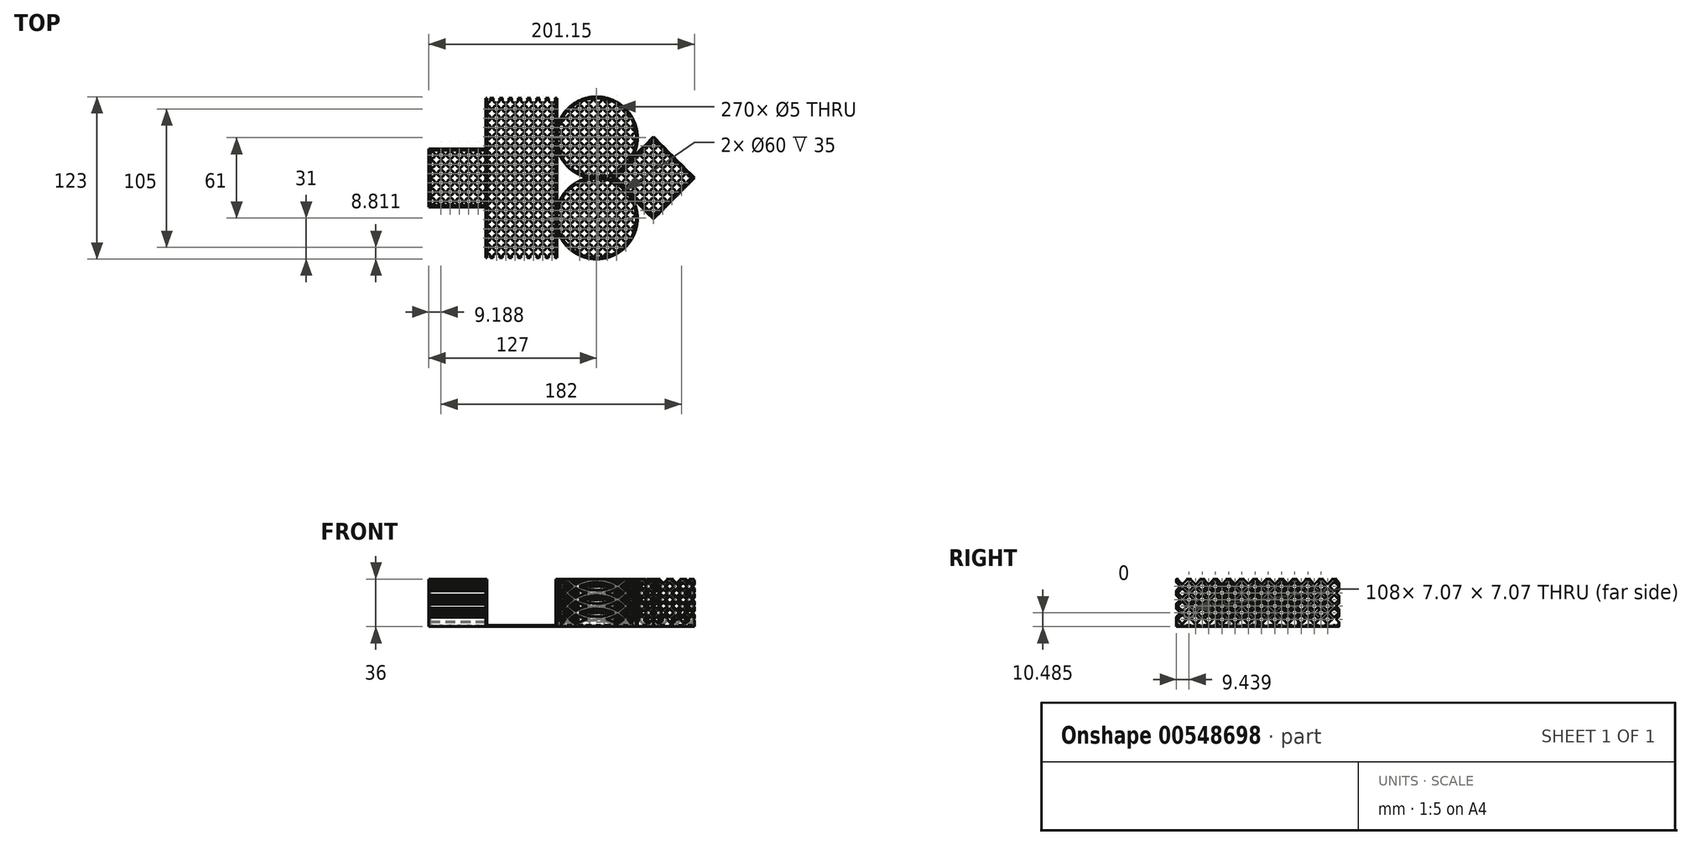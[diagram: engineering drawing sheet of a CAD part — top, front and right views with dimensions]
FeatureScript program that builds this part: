
annotation { "Feature Type Name" : "Feature", "Feature Type Description" : "" }
export const myFeature = defineFeature(function(context is Context, id is Id, definition is map)
    precondition{}
    {
        {
            assignVariable(context, id + "F0", {"name" : "thickness", "anyValue" : 1 * mm});
        }
        {
            var Q0;
            Q0=qCreatedBy(makeId("Top.planeOp"),FACE);
            var sketch = newSketch(context, id + "F1", { "sketchPlane" : qUnion([Q0])});
            skCircle(sketch, "E0", {"center": v(30, 30.5) * mm, "radius": 30 * mm});
            skCircle(sketch, "E1", {"center": v(30, -30.5) * mm, "radius": 30 * mm});
            skLineSegment(sketch, "E2.bottom", {"start": v(43.34, 0) * mm, "end": v(73.04, 29.7) * mm});
            skLineSegment(sketch, "E2.top", {"start": v(73.04, -29.7) * mm, "end": v(102.74, 0) * mm});
            skLineSegment(sketch, "E2.left", {"start": v(43.34, 0) * mm, "end": v(73.04, -29.7) * mm});
            skLineSegment(sketch, "E2.right", {"start": v(73.04, 29.7) * mm, "end": v(102.74, 0) * mm});
            skLineSegment(sketch, "E3.bottom", {"start": v(-53, 60.5) * mm, "end": v(-1, 60.5) * mm});
            skLineSegment(sketch, "E3.top", {"start": v(-53, -60.5) * mm, "end": v(-1, -60.5) * mm});
            skLineSegment(sketch, "E3.left", {"start": v(-53, 60.5) * mm, "end": v(-53, -60.5) * mm});
            skLineSegment(sketch, "E3.right", {"start": v(-1, 60.5) * mm, "end": v(-1, -60.5) * mm});
            skLineSegment(sketch, "E4.bottom", {"start": v(-96, 21) * mm, "end": v(-54, 21) * mm});
            skLineSegment(sketch, "E4.top", {"start": v(-96, -21) * mm, "end": v(-54, -21) * mm});
            skLineSegment(sketch, "E4.left", {"start": v(-96, 21) * mm, "end": v(-96, -21) * mm});
            skLineSegment(sketch, "E4.right", {"start": v(-54, 21) * mm, "end": v(-54, -21) * mm});
            skPoint(sketch, "E5", {"position": v(-96, 0) * mm});
            skSolve(sketch);
        }
        {
            var Q0;
            Q0 = qSketchRegion(id + "F1", true);
            extrude(context, id + "F2", {"entities" : qUnion([Q0]), "depth" : 35 * mm, "offsetDistance" : 25 * mm});
        }
        {
            var Q0;
            Q0=makeQuery(id+"F2.opExtrude","CAP_FACE",FACE,{"disambiguationData":[OSD([sQuery(id+"F1.wireOp",EDGE,"E1")])],"isStart":false});
            var Q1;
            Q1=makeQuery(id+"F2.opExtrude","CAP_FACE",FACE,{"disambiguationData":[OSD([sQuery(id+"F1.wireOp",EDGE,"E3.bottom"),sQuery(id+"F1.wireOp",EDGE,"E3.top"),sQuery(id+"F1.wireOp",EDGE,"E3.left"),sQuery(id+"F1.wireOp",EDGE,"E3.right")])],"isStart":false});
            var Q2;
            Q2=makeQuery(id+"F2.opExtrude","CAP_FACE",FACE,{"disambiguationData":[OSD([sQuery(id+"F1.wireOp",EDGE,"E0")])],"isStart":false});
            var Q3;
            Q3=makeQuery(id+"F2.opExtrude","CAP_FACE",FACE,{"disambiguationData":[OSD([sQuery(id+"F1.wireOp",EDGE,"E2.bottom"),sQuery(id+"F1.wireOp",EDGE,"E2.top"),sQuery(id+"F1.wireOp",EDGE,"E2.left"),sQuery(id+"F1.wireOp",EDGE,"E2.right")])],"isStart":false});
            var Q4;
            Q4=makeQuery(id+"F2.opExtrude","SWEPT_FACE",FACE,{"disambiguationData":[OSD([sQuery(id+"F1.wireOp",EDGE,"E3.bottom")])]});
            var Q5;
            Q5=makeQuery(id+"F2.opExtrude","SWEPT_FACE",FACE,{"disambiguationData":[OSD([sQuery(id+"F1.wireOp",EDGE,"E3.top")])]});
            var Q6;
            Q6=makeQuery(id+"F2.opExtrude","CAP_FACE",FACE,{"disambiguationData":[OSD([sQuery(id+"F1.wireOp",EDGE,"E4.bottom"),sQuery(id+"F1.wireOp",EDGE,"E4.top"),sQuery(id+"F1.wireOp",EDGE,"E4.left"),sQuery(id+"F1.wireOp",EDGE,"E4.right")])],"isStart":false});
            shell(context, id + "F3", {"entities" : qUnion([Q0, Q1, Q2, Q3, Q4, Q5, Q6]), "thickness" : (getVariable(context, 'thickness')), "oppositeDirection" : true});
        }
        {
            var Q0;
            Q0=makeQuery(id+"F2.opExtrude","SWEPT_FACE",FACE,{"disambiguationData":[OSD([sQuery(id+"F1.wireOp",EDGE,"E4.left")])]});
            var sketch = newSketch(context, id + "F4", { "sketchPlane" : qUnion([Q0])});
            skCircle(sketch, "E6", {"center": v(0, 21) * mm, "radius": 17 * mm});
            skLineSegment(sketch, "E7", {"start": v(-17, 21.3) * mm, "end": v(-16.76, 35) * mm});
            skLineSegment(sketch, "E8", {"start": v(17, 21) * mm, "end": v(17, 35) * mm});
            skLineSegment(sketch, "E9", {"start": v(-16.76, 35) * mm, "end": v(17, 35) * mm});
            skSolve(sketch);
        }
        {
            var Q0;
            Q0 = qSketchRegion(id + "F4", true);
            var Q1;
            Q1=makeQuery(id+"F3.opShell","OFFSET_FACE",FACE,{"disambiguationData":[OSD([sQuery(id+"F1.wireOp",EDGE,"E4.left")])]});
            extrude(context, id + "F5", {"entities" : qUnion([Q0]), "operationType" : NewBodyOperationType.REMOVE, "endBound" : BoundingType.UP_TO_SURFACE, "oppositeDirection" : true, "depth" : 25 * mm, "endBoundEntityFace" : qUnion([Q1]), "offsetDistance" : 25 * mm});
        }
        {
            var Q0;
            Q0=makeQuery(id+"F2.opExtrude","SWEPT_FACE",FACE,{"disambiguationData":[OSD([sQuery(id+"F1.wireOp",EDGE,"E2.top")])]});
            var sketch = newSketch(context, id + "F6", { "sketchPlane" : qUnion([Q0])});
            skCircle(sketch, "E10", {"center": v(51.65, 21) * mm, "radius": 17 * mm});
            skLineSegment(sketch, "E11", {"start": v(34.65, 21) * mm, "end": v(34.65, 35) * mm});
            skLineSegment(sketch, "E12", {"start": v(34.65, 35) * mm, "end": v(68.65, 35) * mm});
            skLineSegment(sketch, "E13", {"start": v(68.65, 35) * mm, "end": v(68.65, 21) * mm});
            skSolve(sketch);
        }
        {
            var Q0;
            Q0 = qSketchRegion(id + "F6", true);
            var Q1;
            Q1=makeQuery(id+"F3.opShell","OFFSET_FACE",FACE,{"disambiguationData":[OSD([sQuery(id+"F1.wireOp",EDGE,"E2.top")])]});
            extrude(context, id + "F7", {"entities" : qUnion([Q0]), "operationType" : NewBodyOperationType.REMOVE, "endBound" : BoundingType.UP_TO_SURFACE, "oppositeDirection" : true, "depth" : 25 * mm, "endBoundEntityFace" : qUnion([Q1]), "offsetDistance" : 25 * mm});
        }
        {
            var Q0;
            Q0=makeQuery(id+"F2.opExtrude","CAP_EDGE",EDGE,{"disambiguationData":[OSD([sQuery(id+"F1.wireOp",EDGE,"E3.top")])],"isStart":false});
            var Q1;
            {var subQ0=sQuery(id+"F1.wireOp",EDGE,"E3.top");Q1=makeQuery(id+"F3.opShell","OFFSET_EDGE",EDGE,{"disambiguationData":[OSD([subQ0]),TDD([makeQuery(id+"F2.opExtrude","CAP_EDGE",EDGE,{"disambiguationData":[OSD([subQ0])],"isStart":false})])]});}
            var Q2;
            Q2=makeQuery(id+"F5.boolean.opBoolean","COPY",EDGE,{"derivedFrom":makeQuery(id+"F5.opExtrude","SWEPT_EDGE",EDGE,{"disambiguationData":[OSD([sQuery(id+"F1.wireOp",EDGE,"E4.left"),sQuery(id+"F4.wireOp",EDGE,"E7"),sQuery(id+"F4.wireOp",EDGE,"E9")])]})});
            var Q3;
            Q3=makeQuery(id+"F5.boolean.opBoolean","COPY",EDGE,{"derivedFrom":makeQuery(id+"F5.opExtrude","SWEPT_EDGE",EDGE,{"disambiguationData":[OSD([sQuery(id+"F1.wireOp",EDGE,"E4.left"),sQuery(id+"F4.wireOp",EDGE,"E8"),sQuery(id+"F4.wireOp",EDGE,"E9")])]})});
            var Q4;
            Q4=makeQuery(id+"F2.opExtrude","CAP_EDGE",EDGE,{"disambiguationData":[OSD([sQuery(id+"F1.wireOp",EDGE,"E3.bottom")])],"isStart":false});
            var Q5;
            {var subQ0=sQuery(id+"F1.wireOp",EDGE,"E3.bottom");Q5=makeQuery(id+"F3.opShell","OFFSET_EDGE",EDGE,{"disambiguationData":[OSD([subQ0]),TDD([makeQuery(id+"F2.opExtrude","CAP_EDGE",EDGE,{"disambiguationData":[OSD([subQ0])],"isStart":false})])]});}
            var Q6;
            Q6=makeQuery(id+"F7.boolean.opBoolean","COPY",EDGE,{"derivedFrom":makeQuery(id+"F7.opExtrude","SWEPT_EDGE",EDGE,{"disambiguationData":[OSD([sQuery(id+"F1.wireOp",EDGE,"E2.top"),sQuery(id+"F6.wireOp",EDGE,"E11"),sQuery(id+"F6.wireOp",EDGE,"E12")])]})});
            var Q7;
            Q7=makeQuery(id+"F7.boolean.opBoolean","COPY",EDGE,{"derivedFrom":makeQuery(id+"F7.opExtrude","SWEPT_EDGE",EDGE,{"disambiguationData":[OSD([sQuery(id+"F1.wireOp",EDGE,"E2.top"),sQuery(id+"F6.wireOp",EDGE,"E12"),sQuery(id+"F6.wireOp",EDGE,"E13")])]})});
            fillet(context, id + "F8", {"entities" : qUnion([Q0, Q1, Q2, Q3, Q4, Q5, Q6, Q7]), "radius" : 5 * mm, "tangentPropagation" : true, "allowEdgeOverflow" : false});
        }
        {
            var Q0;
            Q0=makeQuery(id+"F2.opExtrude","SWEPT_BODY",BODY,{"disambiguationData":[OSD([sQuery(id+"F1.wireOp",EDGE,"E0")])]});
            var Q1;
            Q1=makeQuery(id+"F2.opExtrude","SWEPT_BODY",BODY,{"disambiguationData":[OSD([sQuery(id+"F1.wireOp",EDGE,"E1")])]});
            var Q2;
            Q2=makeQuery(id+"F2.opExtrude","SWEPT_BODY",BODY,{"disambiguationData":[OSD([sQuery(id+"F1.wireOp",EDGE,"E3.bottom"),sQuery(id+"F1.wireOp",EDGE,"E3.top"),sQuery(id+"F1.wireOp",EDGE,"E3.left"),sQuery(id+"F1.wireOp",EDGE,"E3.right")])]});
            var Q3;
            Q3=makeQuery(id+"F2.opExtrude","SWEPT_BODY",BODY,{"disambiguationData":[OSD([sQuery(id+"F1.wireOp",EDGE,"E2.bottom"),sQuery(id+"F1.wireOp",EDGE,"E2.top"),sQuery(id+"F1.wireOp",EDGE,"E2.left"),sQuery(id+"F1.wireOp",EDGE,"E2.right")])]});
            var Q4;
            Q4=makeQuery(id+"F2.opExtrude","SWEPT_BODY",BODY,{"disambiguationData":[OSD([sQuery(id+"F1.wireOp",EDGE,"E4.bottom"),sQuery(id+"F1.wireOp",EDGE,"E4.top"),sQuery(id+"F1.wireOp",EDGE,"E4.left"),sQuery(id+"F1.wireOp",EDGE,"E4.right")])]});
            booleanBodies(context, id + "F9", {"operationType" : BooleanOperationType.UNION, "tools" : qUnion([Q0, Q1, Q2, Q3, Q4])});
        }
        {
            var Q0;
            Q0=makeQuery(id+"F9.opBoolean","MERGE",FACE,{"derivedFrom":[makeQuery(id+"F2.opExtrude","CAP_FACE",FACE,{"disambiguationData":[OSD([sQuery(id+"F1.wireOp",EDGE,"E0")])],"isStart":true}),makeQuery(id+"F2.opExtrude","CAP_FACE",FACE,{"disambiguationData":[OSD([sQuery(id+"F1.wireOp",EDGE,"E1")])],"isStart":true}),makeQuery(id+"F2.opExtrude","CAP_FACE",FACE,{"disambiguationData":[OSD([sQuery(id+"F1.wireOp",EDGE,"E2.bottom"),sQuery(id+"F1.wireOp",EDGE,"E2.top"),sQuery(id+"F1.wireOp",EDGE,"E2.left"),sQuery(id+"F1.wireOp",EDGE,"E2.right")])],"isStart":true}),makeQuery(id+"F2.opExtrude","CAP_FACE",FACE,{"disambiguationData":[OSD([sQuery(id+"F1.wireOp",EDGE,"E3.bottom"),sQuery(id+"F1.wireOp",EDGE,"E3.top"),sQuery(id+"F1.wireOp",EDGE,"E3.left"),sQuery(id+"F1.wireOp",EDGE,"E3.right")])],"isStart":true}),makeQuery(id+"F2.opExtrude","CAP_FACE",FACE,{"disambiguationData":[OSD([sQuery(id+"F1.wireOp",EDGE,"E4.bottom"),sQuery(id+"F1.wireOp",EDGE,"E4.top"),sQuery(id+"F1.wireOp",EDGE,"E4.left"),sQuery(id+"F1.wireOp",EDGE,"E4.right")])],"isStart":true})]});
            var sketch = newSketch(context, id + "F10", { "sketchPlane" : qUnion([Q0])});
            skCircle(sketch, "E14", {"center": v(-101.81, -59.31) * mm, "radius": 2.5 * mm});
            skCircle(sketch, "E15.0.1.0", {"center": v(-101.81, -52.31) * mm, "radius": 2.5 * mm});
            skCircle(sketch, "E15.0.2.0", {"center": v(-101.81, -45.31) * mm, "radius": 2.5 * mm});
            skCircle(sketch, "E15.0.3.0", {"center": v(-101.81, -38.31) * mm, "radius": 2.5 * mm});
            skCircle(sketch, "E15.0.4.0", {"center": v(-101.81, -31.31) * mm, "radius": 2.5 * mm});
            skCircle(sketch, "E15.0.5.0", {"center": v(-101.81, -24.31) * mm, "radius": 2.5 * mm});
            skCircle(sketch, "E15.0.6.0", {"center": v(-101.81, -17.31) * mm, "radius": 2.5 * mm});
            skCircle(sketch, "E15.0.7.0", {"center": v(-101.81, -10.31) * mm, "radius": 2.5 * mm});
            skCircle(sketch, "E15.0.8.0", {"center": v(-101.81, -3.31) * mm, "radius": 2.5 * mm});
            skCircle(sketch, "E15.0.9.0", {"center": v(-101.81, 3.69) * mm, "radius": 2.5 * mm});
            skCircle(sketch, "E15.0.10.0", {"center": v(-101.81, 10.69) * mm, "radius": 2.5 * mm});
            skCircle(sketch, "E15.0.11.0", {"center": v(-101.81, 17.69) * mm, "radius": 2.5 * mm});
            skCircle(sketch, "E15.1.0.0", {"center": v(-94.81, -59.31) * mm, "radius": 2.5 * mm});
            skCircle(sketch, "E15.1.1.0", {"center": v(-94.81, -52.31) * mm, "radius": 2.5 * mm});
            skCircle(sketch, "E15.1.2.0", {"center": v(-94.81, -45.31) * mm, "radius": 2.5 * mm});
            skCircle(sketch, "E15.1.3.0", {"center": v(-94.81, -38.31) * mm, "radius": 2.5 * mm});
            skCircle(sketch, "E15.1.4.0", {"center": v(-94.81, -31.31) * mm, "radius": 2.5 * mm});
            skCircle(sketch, "E15.1.5.0", {"center": v(-94.81, -24.31) * mm, "radius": 2.5 * mm});
            skCircle(sketch, "E15.1.6.0", {"center": v(-94.81, -17.31) * mm, "radius": 2.5 * mm});
            skCircle(sketch, "E15.1.7.0", {"center": v(-94.81, -10.31) * mm, "radius": 2.5 * mm});
            skCircle(sketch, "E15.1.8.0", {"center": v(-94.81, -3.31) * mm, "radius": 2.5 * mm});
            skCircle(sketch, "E15.1.9.0", {"center": v(-94.81, 3.69) * mm, "radius": 2.5 * mm});
            skCircle(sketch, "E15.1.10.0", {"center": v(-94.81, 10.69) * mm, "radius": 2.5 * mm});
            skCircle(sketch, "E15.1.11.0", {"center": v(-94.81, 17.69) * mm, "radius": 2.5 * mm});
            skCircle(sketch, "E15.2.0.0", {"center": v(-87.81, -59.31) * mm, "radius": 2.5 * mm});
            skCircle(sketch, "E15.2.1.0", {"center": v(-87.81, -52.31) * mm, "radius": 2.5 * mm});
            skCircle(sketch, "E15.2.2.0", {"center": v(-87.81, -45.31) * mm, "radius": 2.5 * mm});
            skCircle(sketch, "E15.2.3.0", {"center": v(-87.81, -38.31) * mm, "radius": 2.5 * mm});
            skCircle(sketch, "E15.2.4.0", {"center": v(-87.81, -31.31) * mm, "radius": 2.5 * mm});
            skCircle(sketch, "E15.2.5.0", {"center": v(-87.81, -24.31) * mm, "radius": 2.5 * mm});
            skCircle(sketch, "E15.2.6.0", {"center": v(-87.81, -17.31) * mm, "radius": 2.5 * mm});
            skCircle(sketch, "E15.2.7.0", {"center": v(-87.81, -10.31) * mm, "radius": 2.5 * mm});
            skCircle(sketch, "E15.2.8.0", {"center": v(-87.81, -3.31) * mm, "radius": 2.5 * mm});
            skCircle(sketch, "E15.2.9.0", {"center": v(-87.81, 3.69) * mm, "radius": 2.5 * mm});
            skCircle(sketch, "E15.2.10.0", {"center": v(-87.81, 10.69) * mm, "radius": 2.5 * mm});
            skCircle(sketch, "E15.2.11.0", {"center": v(-87.81, 17.69) * mm, "radius": 2.5 * mm});
            skCircle(sketch, "E15.3.0.0", {"center": v(-80.81, -59.31) * mm, "radius": 2.5 * mm});
            skCircle(sketch, "E15.3.1.0", {"center": v(-80.81, -52.31) * mm, "radius": 2.5 * mm});
            skCircle(sketch, "E15.3.2.0", {"center": v(-80.81, -45.31) * mm, "radius": 2.5 * mm});
            skCircle(sketch, "E15.3.3.0", {"center": v(-80.81, -38.31) * mm, "radius": 2.5 * mm});
            skCircle(sketch, "E15.3.4.0", {"center": v(-80.81, -31.31) * mm, "radius": 2.5 * mm});
            skCircle(sketch, "E15.3.5.0", {"center": v(-80.81, -24.31) * mm, "radius": 2.5 * mm});
            skCircle(sketch, "E15.3.6.0", {"center": v(-80.81, -17.31) * mm, "radius": 2.5 * mm});
            skCircle(sketch, "E15.3.7.0", {"center": v(-80.81, -10.31) * mm, "radius": 2.5 * mm});
            skCircle(sketch, "E15.3.8.0", {"center": v(-80.81, -3.31) * mm, "radius": 2.5 * mm});
            skCircle(sketch, "E15.3.9.0", {"center": v(-80.81, 3.69) * mm, "radius": 2.5 * mm});
            skCircle(sketch, "E15.3.10.0", {"center": v(-80.81, 10.69) * mm, "radius": 2.5 * mm});
            skCircle(sketch, "E15.3.11.0", {"center": v(-80.81, 17.69) * mm, "radius": 2.5 * mm});
            skCircle(sketch, "E15.4.0.0", {"center": v(-73.81, -59.31) * mm, "radius": 2.5 * mm});
            skCircle(sketch, "E15.4.1.0", {"center": v(-73.81, -52.31) * mm, "radius": 2.5 * mm});
            skCircle(sketch, "E15.4.2.0", {"center": v(-73.81, -45.31) * mm, "radius": 2.5 * mm});
            skCircle(sketch, "E15.4.3.0", {"center": v(-73.81, -38.31) * mm, "radius": 2.5 * mm});
            skCircle(sketch, "E15.4.4.0", {"center": v(-73.81, -31.31) * mm, "radius": 2.5 * mm});
            skCircle(sketch, "E15.4.5.0", {"center": v(-73.81, -24.31) * mm, "radius": 2.5 * mm});
            skCircle(sketch, "E15.4.6.0", {"center": v(-73.81, -17.31) * mm, "radius": 2.5 * mm});
            skCircle(sketch, "E15.4.7.0", {"center": v(-73.81, -10.31) * mm, "radius": 2.5 * mm});
            skCircle(sketch, "E15.4.8.0", {"center": v(-73.81, -3.31) * mm, "radius": 2.5 * mm});
            skCircle(sketch, "E15.4.9.0", {"center": v(-73.81, 3.69) * mm, "radius": 2.5 * mm});
            skCircle(sketch, "E15.4.10.0", {"center": v(-73.81, 10.69) * mm, "radius": 2.5 * mm});
            skCircle(sketch, "E15.4.11.0", {"center": v(-73.81, 17.69) * mm, "radius": 2.5 * mm});
            skCircle(sketch, "E15.5.0.0", {"center": v(-66.81, -59.31) * mm, "radius": 2.5 * mm});
            skCircle(sketch, "E15.5.1.0", {"center": v(-66.81, -52.31) * mm, "radius": 2.5 * mm});
            skCircle(sketch, "E15.5.2.0", {"center": v(-66.81, -45.31) * mm, "radius": 2.5 * mm});
            skCircle(sketch, "E15.5.3.0", {"center": v(-66.81, -38.31) * mm, "radius": 2.5 * mm});
            skCircle(sketch, "E15.5.4.0", {"center": v(-66.81, -31.31) * mm, "radius": 2.5 * mm});
            skCircle(sketch, "E15.5.5.0", {"center": v(-66.81, -24.31) * mm, "radius": 2.5 * mm});
            skCircle(sketch, "E15.5.6.0", {"center": v(-66.81, -17.31) * mm, "radius": 2.5 * mm});
            skCircle(sketch, "E15.5.7.0", {"center": v(-66.81, -10.31) * mm, "radius": 2.5 * mm});
            skCircle(sketch, "E15.5.8.0", {"center": v(-66.81, -3.31) * mm, "radius": 2.5 * mm});
            skCircle(sketch, "E15.5.9.0", {"center": v(-66.81, 3.69) * mm, "radius": 2.5 * mm});
            skCircle(sketch, "E15.5.10.0", {"center": v(-66.81, 10.69) * mm, "radius": 2.5 * mm});
            skCircle(sketch, "E15.5.11.0", {"center": v(-66.81, 17.69) * mm, "radius": 2.5 * mm});
            skCircle(sketch, "E15.6.0.0", {"center": v(-59.81, -59.31) * mm, "radius": 2.5 * mm});
            skCircle(sketch, "E15.6.1.0", {"center": v(-59.81, -52.31) * mm, "radius": 2.5 * mm});
            skCircle(sketch, "E15.6.2.0", {"center": v(-59.81, -45.31) * mm, "radius": 2.5 * mm});
            skCircle(sketch, "E15.6.3.0", {"center": v(-59.81, -38.31) * mm, "radius": 2.5 * mm});
            skCircle(sketch, "E15.6.4.0", {"center": v(-59.81, -31.31) * mm, "radius": 2.5 * mm});
            skCircle(sketch, "E15.6.5.0", {"center": v(-59.81, -24.31) * mm, "radius": 2.5 * mm});
            skCircle(sketch, "E15.6.6.0", {"center": v(-59.81, -17.31) * mm, "radius": 2.5 * mm});
            skCircle(sketch, "E15.6.7.0", {"center": v(-59.81, -10.31) * mm, "radius": 2.5 * mm});
            skCircle(sketch, "E15.6.8.0", {"center": v(-59.81, -3.31) * mm, "radius": 2.5 * mm});
            skCircle(sketch, "E15.6.9.0", {"center": v(-59.81, 3.69) * mm, "radius": 2.5 * mm});
            skCircle(sketch, "E15.6.10.0", {"center": v(-59.81, 10.69) * mm, "radius": 2.5 * mm});
            skCircle(sketch, "E15.6.11.0", {"center": v(-59.81, 17.69) * mm, "radius": 2.5 * mm});
            skCircle(sketch, "E15.7.0.0", {"center": v(-52.81, -59.31) * mm, "radius": 2.5 * mm});
            skCircle(sketch, "E15.7.1.0", {"center": v(-52.81, -52.31) * mm, "radius": 2.5 * mm});
            skCircle(sketch, "E15.7.2.0", {"center": v(-52.81, -45.31) * mm, "radius": 2.5 * mm});
            skCircle(sketch, "E15.7.3.0", {"center": v(-52.81, -38.31) * mm, "radius": 2.5 * mm});
            skCircle(sketch, "E15.7.4.0", {"center": v(-52.81, -31.31) * mm, "radius": 2.5 * mm});
            skCircle(sketch, "E15.7.5.0", {"center": v(-52.81, -24.31) * mm, "radius": 2.5 * mm});
            skCircle(sketch, "E15.7.6.0", {"center": v(-52.81, -17.31) * mm, "radius": 2.5 * mm});
            skCircle(sketch, "E15.7.7.0", {"center": v(-52.81, -10.31) * mm, "radius": 2.5 * mm});
            skCircle(sketch, "E15.7.8.0", {"center": v(-52.81, -3.31) * mm, "radius": 2.5 * mm});
            skCircle(sketch, "E15.7.9.0", {"center": v(-52.81, 3.69) * mm, "radius": 2.5 * mm});
            skCircle(sketch, "E15.7.10.0", {"center": v(-52.81, 10.69) * mm, "radius": 2.5 * mm});
            skCircle(sketch, "E15.7.11.0", {"center": v(-52.81, 17.69) * mm, "radius": 2.5 * mm});
            skCircle(sketch, "E15.8.0.0", {"center": v(-45.81, -59.31) * mm, "radius": 2.5 * mm});
            skCircle(sketch, "E15.8.1.0", {"center": v(-45.81, -52.31) * mm, "radius": 2.5 * mm});
            skCircle(sketch, "E15.8.2.0", {"center": v(-45.81, -45.31) * mm, "radius": 2.5 * mm});
            skCircle(sketch, "E15.8.3.0", {"center": v(-45.81, -38.31) * mm, "radius": 2.5 * mm});
            skCircle(sketch, "E15.8.4.0", {"center": v(-45.81, -31.31) * mm, "radius": 2.5 * mm});
            skCircle(sketch, "E15.8.5.0", {"center": v(-45.81, -24.31) * mm, "radius": 2.5 * mm});
            skCircle(sketch, "E15.8.6.0", {"center": v(-45.81, -17.31) * mm, "radius": 2.5 * mm});
            skCircle(sketch, "E15.8.7.0", {"center": v(-45.81, -10.31) * mm, "radius": 2.5 * mm});
            skCircle(sketch, "E15.8.8.0", {"center": v(-45.81, -3.31) * mm, "radius": 2.5 * mm});
            skCircle(sketch, "E15.8.9.0", {"center": v(-45.81, 3.69) * mm, "radius": 2.5 * mm});
            skCircle(sketch, "E15.8.10.0", {"center": v(-45.81, 10.69) * mm, "radius": 2.5 * mm});
            skCircle(sketch, "E15.8.11.0", {"center": v(-45.81, 17.69) * mm, "radius": 2.5 * mm});
            skCircle(sketch, "E15.9.0.0", {"center": v(-38.81, -59.31) * mm, "radius": 2.5 * mm});
            skCircle(sketch, "E15.9.1.0", {"center": v(-38.81, -52.31) * mm, "radius": 2.5 * mm});
            skCircle(sketch, "E15.9.2.0", {"center": v(-38.81, -45.31) * mm, "radius": 2.5 * mm});
            skCircle(sketch, "E15.9.3.0", {"center": v(-38.81, -38.31) * mm, "radius": 2.5 * mm});
            skCircle(sketch, "E15.9.4.0", {"center": v(-38.81, -31.31) * mm, "radius": 2.5 * mm});
            skCircle(sketch, "E15.9.5.0", {"center": v(-38.81, -24.31) * mm, "radius": 2.5 * mm});
            skCircle(sketch, "E15.9.6.0", {"center": v(-38.81, -17.31) * mm, "radius": 2.5 * mm});
            skCircle(sketch, "E15.9.7.0", {"center": v(-38.81, -10.31) * mm, "radius": 2.5 * mm});
            skCircle(sketch, "E15.9.8.0", {"center": v(-38.81, -3.31) * mm, "radius": 2.5 * mm});
            skCircle(sketch, "E15.9.9.0", {"center": v(-38.81, 3.69) * mm, "radius": 2.5 * mm});
            skCircle(sketch, "E15.9.10.0", {"center": v(-38.81, 10.69) * mm, "radius": 2.5 * mm});
            skCircle(sketch, "E15.9.11.0", {"center": v(-38.81, 17.69) * mm, "radius": 2.5 * mm});
            skCircle(sketch, "E15.10.0.0", {"center": v(-31.81, -59.31) * mm, "radius": 2.5 * mm});
            skCircle(sketch, "E15.10.1.0", {"center": v(-31.81, -52.31) * mm, "radius": 2.5 * mm});
            skCircle(sketch, "E15.10.2.0", {"center": v(-31.81, -45.31) * mm, "radius": 2.5 * mm});
            skCircle(sketch, "E15.10.3.0", {"center": v(-31.81, -38.31) * mm, "radius": 2.5 * mm});
            skCircle(sketch, "E15.10.4.0", {"center": v(-31.81, -31.31) * mm, "radius": 2.5 * mm});
            skCircle(sketch, "E15.10.5.0", {"center": v(-31.81, -24.31) * mm, "radius": 2.5 * mm});
            skCircle(sketch, "E15.10.6.0", {"center": v(-31.81, -17.31) * mm, "radius": 2.5 * mm});
            skCircle(sketch, "E15.10.7.0", {"center": v(-31.81, -10.31) * mm, "radius": 2.5 * mm});
            skCircle(sketch, "E15.10.8.0", {"center": v(-31.81, -3.31) * mm, "radius": 2.5 * mm});
            skCircle(sketch, "E15.10.9.0", {"center": v(-31.81, 3.69) * mm, "radius": 2.5 * mm});
            skCircle(sketch, "E15.10.10.0", {"center": v(-31.81, 10.69) * mm, "radius": 2.5 * mm});
            skCircle(sketch, "E15.10.11.0", {"center": v(-31.81, 17.69) * mm, "radius": 2.5 * mm});
            skCircle(sketch, "E15.11.0.0", {"center": v(-24.81, -59.31) * mm, "radius": 2.5 * mm});
            skCircle(sketch, "E15.11.1.0", {"center": v(-24.81, -52.31) * mm, "radius": 2.5 * mm});
            skCircle(sketch, "E15.11.2.0", {"center": v(-24.81, -45.31) * mm, "radius": 2.5 * mm});
            skCircle(sketch, "E15.11.3.0", {"center": v(-24.81, -38.31) * mm, "radius": 2.5 * mm});
            skCircle(sketch, "E15.11.4.0", {"center": v(-24.81, -31.31) * mm, "radius": 2.5 * mm});
            skCircle(sketch, "E15.11.5.0", {"center": v(-24.81, -24.31) * mm, "radius": 2.5 * mm});
            skCircle(sketch, "E15.11.6.0", {"center": v(-24.81, -17.31) * mm, "radius": 2.5 * mm});
            skCircle(sketch, "E15.11.7.0", {"center": v(-24.81, -10.31) * mm, "radius": 2.5 * mm});
            skCircle(sketch, "E15.11.8.0", {"center": v(-24.81, -3.31) * mm, "radius": 2.5 * mm});
            skCircle(sketch, "E15.11.9.0", {"center": v(-24.81, 3.69) * mm, "radius": 2.5 * mm});
            skCircle(sketch, "E15.11.10.0", {"center": v(-24.81, 10.69) * mm, "radius": 2.5 * mm});
            skCircle(sketch, "E15.11.11.0", {"center": v(-24.81, 17.69) * mm, "radius": 2.5 * mm});
            skCircle(sketch, "E15.12.0.0", {"center": v(-17.81, -59.31) * mm, "radius": 2.5 * mm});
            skCircle(sketch, "E15.12.1.0", {"center": v(-17.81, -52.31) * mm, "radius": 2.5 * mm});
            skCircle(sketch, "E15.12.2.0", {"center": v(-17.81, -45.31) * mm, "radius": 2.5 * mm});
            skCircle(sketch, "E15.12.3.0", {"center": v(-17.81, -38.31) * mm, "radius": 2.5 * mm});
            skCircle(sketch, "E15.12.4.0", {"center": v(-17.81, -31.31) * mm, "radius": 2.5 * mm});
            skCircle(sketch, "E15.12.5.0", {"center": v(-17.81, -24.31) * mm, "radius": 2.5 * mm});
            skCircle(sketch, "E15.12.6.0", {"center": v(-17.81, -17.31) * mm, "radius": 2.5 * mm});
            skCircle(sketch, "E15.12.7.0", {"center": v(-17.81, -10.31) * mm, "radius": 2.5 * mm});
            skCircle(sketch, "E15.12.8.0", {"center": v(-17.81, -3.31) * mm, "radius": 2.5 * mm});
            skCircle(sketch, "E15.12.9.0", {"center": v(-17.81, 3.69) * mm, "radius": 2.5 * mm});
            skCircle(sketch, "E15.12.10.0", {"center": v(-17.81, 10.69) * mm, "radius": 2.5 * mm});
            skCircle(sketch, "E15.12.11.0", {"center": v(-17.81, 17.69) * mm, "radius": 2.5 * mm});
            skCircle(sketch, "E15.13.0.0", {"center": v(-10.81, -59.31) * mm, "radius": 2.5 * mm});
            skCircle(sketch, "E15.13.1.0", {"center": v(-10.81, -52.31) * mm, "radius": 2.5 * mm});
            skCircle(sketch, "E15.13.2.0", {"center": v(-10.81, -45.31) * mm, "radius": 2.5 * mm});
            skCircle(sketch, "E15.13.3.0", {"center": v(-10.81, -38.31) * mm, "radius": 2.5 * mm});
            skCircle(sketch, "E15.13.4.0", {"center": v(-10.81, -31.31) * mm, "radius": 2.5 * mm});
            skCircle(sketch, "E15.13.5.0", {"center": v(-10.81, -24.31) * mm, "radius": 2.5 * mm});
            skCircle(sketch, "E15.13.6.0", {"center": v(-10.81, -17.31) * mm, "radius": 2.5 * mm});
            skCircle(sketch, "E15.13.7.0", {"center": v(-10.81, -10.31) * mm, "radius": 2.5 * mm});
            skCircle(sketch, "E15.13.8.0", {"center": v(-10.81, -3.31) * mm, "radius": 2.5 * mm});
            skCircle(sketch, "E15.13.9.0", {"center": v(-10.81, 3.69) * mm, "radius": 2.5 * mm});
            skCircle(sketch, "E15.13.10.0", {"center": v(-10.81, 10.69) * mm, "radius": 2.5 * mm});
            skCircle(sketch, "E15.13.11.0", {"center": v(-10.81, 17.69) * mm, "radius": 2.5 * mm});
            skCircle(sketch, "E15.14.0.0", {"center": v(-3.81, -59.31) * mm, "radius": 2.5 * mm});
            skCircle(sketch, "E15.14.1.0", {"center": v(-3.81, -52.31) * mm, "radius": 2.5 * mm});
            skCircle(sketch, "E15.14.2.0", {"center": v(-3.81, -45.31) * mm, "radius": 2.5 * mm});
            skCircle(sketch, "E15.14.3.0", {"center": v(-3.81, -38.31) * mm, "radius": 2.5 * mm});
            skCircle(sketch, "E15.14.4.0", {"center": v(-3.81, -31.31) * mm, "radius": 2.5 * mm});
            skCircle(sketch, "E15.14.5.0", {"center": v(-3.81, -24.31) * mm, "radius": 2.5 * mm});
            skCircle(sketch, "E15.14.6.0", {"center": v(-3.81, -17.31) * mm, "radius": 2.5 * mm});
            skCircle(sketch, "E15.14.7.0", {"center": v(-3.81, -10.31) * mm, "radius": 2.5 * mm});
            skCircle(sketch, "E15.14.8.0", {"center": v(-3.81, -3.31) * mm, "radius": 2.5 * mm});
            skCircle(sketch, "E15.14.9.0", {"center": v(-3.81, 3.69) * mm, "radius": 2.5 * mm});
            skCircle(sketch, "E15.14.10.0", {"center": v(-3.81, 10.69) * mm, "radius": 2.5 * mm});
            skCircle(sketch, "E15.14.11.0", {"center": v(-3.81, 17.69) * mm, "radius": 2.5 * mm});
            skCircle(sketch, "E15.15.0.0", {"center": v(3.19, -59.31) * mm, "radius": 2.5 * mm});
            skCircle(sketch, "E15.15.1.0", {"center": v(3.19, -52.31) * mm, "radius": 2.5 * mm});
            skCircle(sketch, "E15.15.2.0", {"center": v(3.19, -45.31) * mm, "radius": 2.5 * mm});
            skCircle(sketch, "E15.15.3.0", {"center": v(3.19, -38.31) * mm, "radius": 2.5 * mm});
            skCircle(sketch, "E15.15.4.0", {"center": v(3.19, -31.31) * mm, "radius": 2.5 * mm});
            skCircle(sketch, "E15.15.5.0", {"center": v(3.19, -24.31) * mm, "radius": 2.5 * mm});
            skCircle(sketch, "E15.15.6.0", {"center": v(3.19, -17.31) * mm, "radius": 2.5 * mm});
            skCircle(sketch, "E15.15.7.0", {"center": v(3.19, -10.31) * mm, "radius": 2.5 * mm});
            skCircle(sketch, "E15.15.8.0", {"center": v(3.19, -3.31) * mm, "radius": 2.5 * mm});
            skCircle(sketch, "E15.15.9.0", {"center": v(3.19, 3.69) * mm, "radius": 2.5 * mm});
            skCircle(sketch, "E15.15.10.0", {"center": v(3.19, 10.69) * mm, "radius": 2.5 * mm});
            skCircle(sketch, "E15.15.11.0", {"center": v(3.19, 17.69) * mm, "radius": 2.5 * mm});
            skCircle(sketch, "E15.16.0.0", {"center": v(10.19, -59.31) * mm, "radius": 2.5 * mm});
            skCircle(sketch, "E15.16.1.0", {"center": v(10.19, -52.31) * mm, "radius": 2.5 * mm});
            skCircle(sketch, "E15.16.2.0", {"center": v(10.19, -45.31) * mm, "radius": 2.5 * mm});
            skCircle(sketch, "E15.16.3.0", {"center": v(10.19, -38.31) * mm, "radius": 2.5 * mm});
            skCircle(sketch, "E15.16.4.0", {"center": v(10.19, -31.31) * mm, "radius": 2.5 * mm});
            skCircle(sketch, "E15.16.5.0", {"center": v(10.19, -24.31) * mm, "radius": 2.5 * mm});
            skCircle(sketch, "E15.16.6.0", {"center": v(10.19, -17.31) * mm, "radius": 2.5 * mm});
            skCircle(sketch, "E15.16.7.0", {"center": v(10.19, -10.31) * mm, "radius": 2.5 * mm});
            skCircle(sketch, "E15.16.8.0", {"center": v(10.19, -3.31) * mm, "radius": 2.5 * mm});
            skCircle(sketch, "E15.16.9.0", {"center": v(10.19, 3.69) * mm, "radius": 2.5 * mm});
            skCircle(sketch, "E15.16.10.0", {"center": v(10.19, 10.69) * mm, "radius": 2.5 * mm});
            skCircle(sketch, "E15.16.11.0", {"center": v(10.19, 17.69) * mm, "radius": 2.5 * mm});
            skCircle(sketch, "E15.17.0.0", {"center": v(17.19, -59.31) * mm, "radius": 2.5 * mm});
            skCircle(sketch, "E15.17.1.0", {"center": v(17.19, -52.31) * mm, "radius": 2.5 * mm});
            skCircle(sketch, "E15.17.2.0", {"center": v(17.19, -45.31) * mm, "radius": 2.5 * mm});
            skCircle(sketch, "E15.17.3.0", {"center": v(17.19, -38.31) * mm, "radius": 2.5 * mm});
            skCircle(sketch, "E15.17.4.0", {"center": v(17.19, -31.31) * mm, "radius": 2.5 * mm});
            skCircle(sketch, "E15.17.5.0", {"center": v(17.19, -24.31) * mm, "radius": 2.5 * mm});
            skCircle(sketch, "E15.17.6.0", {"center": v(17.19, -17.31) * mm, "radius": 2.5 * mm});
            skCircle(sketch, "E15.17.7.0", {"center": v(17.19, -10.31) * mm, "radius": 2.5 * mm});
            skCircle(sketch, "E15.17.8.0", {"center": v(17.19, -3.31) * mm, "radius": 2.5 * mm});
            skCircle(sketch, "E15.17.9.0", {"center": v(17.19, 3.69) * mm, "radius": 2.5 * mm});
            skCircle(sketch, "E15.17.10.0", {"center": v(17.19, 10.69) * mm, "radius": 2.5 * mm});
            skCircle(sketch, "E15.17.11.0", {"center": v(17.19, 17.69) * mm, "radius": 2.5 * mm});
            skCircle(sketch, "E15.18.0.0", {"center": v(24.19, -59.31) * mm, "radius": 2.5 * mm});
            skCircle(sketch, "E15.18.1.0", {"center": v(24.19, -52.31) * mm, "radius": 2.5 * mm});
            skCircle(sketch, "E15.18.2.0", {"center": v(24.19, -45.31) * mm, "radius": 2.5 * mm});
            skCircle(sketch, "E15.18.3.0", {"center": v(24.19, -38.31) * mm, "radius": 2.5 * mm});
            skCircle(sketch, "E15.18.4.0", {"center": v(24.19, -31.31) * mm, "radius": 2.5 * mm});
            skCircle(sketch, "E15.18.5.0", {"center": v(24.19, -24.31) * mm, "radius": 2.5 * mm});
            skCircle(sketch, "E15.18.6.0", {"center": v(24.19, -17.31) * mm, "radius": 2.5 * mm});
            skCircle(sketch, "E15.18.7.0", {"center": v(24.19, -10.31) * mm, "radius": 2.5 * mm});
            skCircle(sketch, "E15.18.8.0", {"center": v(24.19, -3.31) * mm, "radius": 2.5 * mm});
            skCircle(sketch, "E15.18.9.0", {"center": v(24.19, 3.69) * mm, "radius": 2.5 * mm});
            skCircle(sketch, "E15.18.10.0", {"center": v(24.19, 10.69) * mm, "radius": 2.5 * mm});
            skCircle(sketch, "E15.18.11.0", {"center": v(24.19, 17.69) * mm, "radius": 2.5 * mm});
            skCircle(sketch, "E15.19.0.0", {"center": v(31.19, -59.31) * mm, "radius": 2.5 * mm});
            skCircle(sketch, "E15.19.1.0", {"center": v(31.19, -52.31) * mm, "radius": 2.5 * mm});
            skCircle(sketch, "E15.19.2.0", {"center": v(31.19, -45.31) * mm, "radius": 2.5 * mm});
            skCircle(sketch, "E15.19.3.0", {"center": v(31.19, -38.31) * mm, "radius": 2.5 * mm});
            skCircle(sketch, "E15.19.4.0", {"center": v(31.19, -31.31) * mm, "radius": 2.5 * mm});
            skCircle(sketch, "E15.19.5.0", {"center": v(31.19, -24.31) * mm, "radius": 2.5 * mm});
            skCircle(sketch, "E15.19.6.0", {"center": v(31.19, -17.31) * mm, "radius": 2.5 * mm});
            skCircle(sketch, "E15.19.7.0", {"center": v(31.19, -10.31) * mm, "radius": 2.5 * mm});
            skCircle(sketch, "E15.19.8.0", {"center": v(31.19, -3.31) * mm, "radius": 2.5 * mm});
            skCircle(sketch, "E15.19.9.0", {"center": v(31.19, 3.69) * mm, "radius": 2.5 * mm});
            skCircle(sketch, "E15.19.10.0", {"center": v(31.19, 10.69) * mm, "radius": 2.5 * mm});
            skCircle(sketch, "E15.19.11.0", {"center": v(31.19, 17.69) * mm, "radius": 2.5 * mm});
            skLineSegment(sketch, "E15.direction1", {"start": v(-101.81, -59.31) * mm, "end": v(-94.81, -59.31) * mm, "construction": true});
            skLineSegment(sketch, "E15.direction2", {"start": v(-101.81, -59.31) * mm, "end": v(-101.81, -52.31) * mm, "construction": true});
            skCircle(sketch, "E16.0.20.0", {"center": v(38.19, -59.31) * mm, "radius": 2.5 * mm});
            skCircle(sketch, "E16.0.20.1", {"center": v(38.19, -52.31) * mm, "radius": 2.5 * mm});
            skCircle(sketch, "E16.0.20.2", {"center": v(38.19, -45.31) * mm, "radius": 2.5 * mm});
            skCircle(sketch, "E16.0.20.3", {"center": v(38.19, -38.31) * mm, "radius": 2.5 * mm});
            skCircle(sketch, "E16.0.20.4", {"center": v(38.19, -31.31) * mm, "radius": 2.5 * mm});
            skCircle(sketch, "E16.0.20.5", {"center": v(38.19, -24.31) * mm, "radius": 2.5 * mm});
            skCircle(sketch, "E16.0.20.6", {"center": v(38.19, -17.31) * mm, "radius": 2.5 * mm});
            skCircle(sketch, "E16.0.20.7", {"center": v(38.19, -10.31) * mm, "radius": 2.5 * mm});
            skCircle(sketch, "E16.0.20.8", {"center": v(38.19, -3.31) * mm, "radius": 2.5 * mm});
            skCircle(sketch, "E16.0.20.9", {"center": v(38.19, 3.69) * mm, "radius": 2.5 * mm});
            skCircle(sketch, "E16.0.20.10", {"center": v(38.19, 10.69) * mm, "radius": 2.5 * mm});
            skCircle(sketch, "E16.0.20.11", {"center": v(38.19, 17.69) * mm, "radius": 2.5 * mm});
            skCircle(sketch, "E16.0.21.0", {"center": v(45.19, -59.31) * mm, "radius": 2.5 * mm});
            skCircle(sketch, "E16.0.21.1", {"center": v(45.19, -52.31) * mm, "radius": 2.5 * mm});
            skCircle(sketch, "E16.0.21.2", {"center": v(45.19, -45.31) * mm, "radius": 2.5 * mm});
            skCircle(sketch, "E16.0.21.3", {"center": v(45.19, -38.31) * mm, "radius": 2.5 * mm});
            skCircle(sketch, "E16.0.21.4", {"center": v(45.19, -31.31) * mm, "radius": 2.5 * mm});
            skCircle(sketch, "E16.0.21.5", {"center": v(45.19, -24.31) * mm, "radius": 2.5 * mm});
            skCircle(sketch, "E16.0.21.6", {"center": v(45.19, -17.31) * mm, "radius": 2.5 * mm});
            skCircle(sketch, "E16.0.21.7", {"center": v(45.19, -10.31) * mm, "radius": 2.5 * mm});
            skCircle(sketch, "E16.0.21.8", {"center": v(45.19, -3.31) * mm, "radius": 2.5 * mm});
            skCircle(sketch, "E16.0.21.9", {"center": v(45.19, 3.69) * mm, "radius": 2.5 * mm});
            skCircle(sketch, "E16.0.21.10", {"center": v(45.19, 10.69) * mm, "radius": 2.5 * mm});
            skCircle(sketch, "E16.0.21.11", {"center": v(45.19, 17.69) * mm, "radius": 2.5 * mm});
            skCircle(sketch, "E17.0.22.0", {"center": v(52.19, -59.31) * mm, "radius": 2.5 * mm});
            skCircle(sketch, "E17.0.22.1", {"center": v(52.19, -52.31) * mm, "radius": 2.5 * mm});
            skCircle(sketch, "E17.0.22.2", {"center": v(52.19, -45.31) * mm, "radius": 2.5 * mm});
            skCircle(sketch, "E17.0.22.3", {"center": v(52.19, -38.31) * mm, "radius": 2.5 * mm});
            skCircle(sketch, "E17.0.22.4", {"center": v(52.19, -31.31) * mm, "radius": 2.5 * mm});
            skCircle(sketch, "E17.0.22.5", {"center": v(52.19, -24.31) * mm, "radius": 2.5 * mm});
            skCircle(sketch, "E17.0.22.6", {"center": v(52.19, -17.31) * mm, "radius": 2.5 * mm});
            skCircle(sketch, "E17.0.22.7", {"center": v(52.19, -10.31) * mm, "radius": 2.5 * mm});
            skCircle(sketch, "E17.0.22.8", {"center": v(52.19, -3.31) * mm, "radius": 2.5 * mm});
            skCircle(sketch, "E17.0.22.9", {"center": v(52.19, 3.69) * mm, "radius": 2.5 * mm});
            skCircle(sketch, "E17.0.22.10", {"center": v(52.19, 10.69) * mm, "radius": 2.5 * mm});
            skCircle(sketch, "E17.0.22.11", {"center": v(52.19, 17.69) * mm, "radius": 2.5 * mm});
            skCircle(sketch, "E17.0.23.0", {"center": v(59.19, -59.31) * mm, "radius": 2.5 * mm});
            skCircle(sketch, "E17.0.23.1", {"center": v(59.19, -52.31) * mm, "radius": 2.5 * mm});
            skCircle(sketch, "E17.0.23.2", {"center": v(59.19, -45.31) * mm, "radius": 2.5 * mm});
            skCircle(sketch, "E17.0.23.3", {"center": v(59.19, -38.31) * mm, "radius": 2.5 * mm});
            skCircle(sketch, "E17.0.23.4", {"center": v(59.19, -31.31) * mm, "radius": 2.5 * mm});
            skCircle(sketch, "E17.0.23.5", {"center": v(59.19, -24.31) * mm, "radius": 2.5 * mm});
            skCircle(sketch, "E17.0.23.6", {"center": v(59.19, -17.31) * mm, "radius": 2.5 * mm});
            skCircle(sketch, "E17.0.23.7", {"center": v(59.19, -10.31) * mm, "radius": 2.5 * mm});
            skCircle(sketch, "E17.0.23.8", {"center": v(59.19, -3.31) * mm, "radius": 2.5 * mm});
            skCircle(sketch, "E17.0.23.9", {"center": v(59.19, 3.69) * mm, "radius": 2.5 * mm});
            skCircle(sketch, "E17.0.23.10", {"center": v(59.19, 10.69) * mm, "radius": 2.5 * mm});
            skCircle(sketch, "E17.0.23.11", {"center": v(59.19, 17.69) * mm, "radius": 2.5 * mm});
            skCircle(sketch, "E17.0.24.0", {"center": v(66.19, -59.31) * mm, "radius": 2.5 * mm});
            skCircle(sketch, "E17.0.24.1", {"center": v(66.19, -52.31) * mm, "radius": 2.5 * mm});
            skCircle(sketch, "E17.0.24.2", {"center": v(66.19, -45.31) * mm, "radius": 2.5 * mm});
            skCircle(sketch, "E17.0.24.3", {"center": v(66.19, -38.31) * mm, "radius": 2.5 * mm});
            skCircle(sketch, "E17.0.24.4", {"center": v(66.19, -31.31) * mm, "radius": 2.5 * mm});
            skCircle(sketch, "E17.0.24.5", {"center": v(66.19, -24.31) * mm, "radius": 2.5 * mm});
            skCircle(sketch, "E17.0.24.6", {"center": v(66.19, -17.31) * mm, "radius": 2.5 * mm});
            skCircle(sketch, "E17.0.24.7", {"center": v(66.19, -10.31) * mm, "radius": 2.5 * mm});
            skCircle(sketch, "E17.0.24.8", {"center": v(66.19, -3.31) * mm, "radius": 2.5 * mm});
            skCircle(sketch, "E17.0.24.9", {"center": v(66.19, 3.69) * mm, "radius": 2.5 * mm});
            skCircle(sketch, "E17.0.24.10", {"center": v(66.19, 10.69) * mm, "radius": 2.5 * mm});
            skCircle(sketch, "E17.0.24.11", {"center": v(66.19, 17.69) * mm, "radius": 2.5 * mm});
            skCircle(sketch, "E17.0.25.0", {"center": v(73.19, -59.31) * mm, "radius": 2.5 * mm});
            skCircle(sketch, "E17.0.25.1", {"center": v(73.19, -52.31) * mm, "radius": 2.5 * mm});
            skCircle(sketch, "E17.0.25.2", {"center": v(73.19, -45.31) * mm, "radius": 2.5 * mm});
            skCircle(sketch, "E17.0.25.3", {"center": v(73.19, -38.31) * mm, "radius": 2.5 * mm});
            skCircle(sketch, "E17.0.25.4", {"center": v(73.19, -31.31) * mm, "radius": 2.5 * mm});
            skCircle(sketch, "E17.0.25.5", {"center": v(73.19, -24.31) * mm, "radius": 2.5 * mm});
            skCircle(sketch, "E17.0.25.6", {"center": v(73.19, -17.31) * mm, "radius": 2.5 * mm});
            skCircle(sketch, "E17.0.25.7", {"center": v(73.19, -10.31) * mm, "radius": 2.5 * mm});
            skCircle(sketch, "E17.0.25.8", {"center": v(73.19, -3.31) * mm, "radius": 2.5 * mm});
            skCircle(sketch, "E17.0.25.9", {"center": v(73.19, 3.69) * mm, "radius": 2.5 * mm});
            skCircle(sketch, "E17.0.25.10", {"center": v(73.19, 10.69) * mm, "radius": 2.5 * mm});
            skCircle(sketch, "E17.0.25.11", {"center": v(73.19, 17.69) * mm, "radius": 2.5 * mm});
            skCircle(sketch, "E17.0.26.0", {"center": v(80.19, -59.31) * mm, "radius": 2.5 * mm});
            skCircle(sketch, "E17.0.26.1", {"center": v(80.19, -52.31) * mm, "radius": 2.5 * mm});
            skCircle(sketch, "E17.0.26.2", {"center": v(80.19, -45.31) * mm, "radius": 2.5 * mm});
            skCircle(sketch, "E17.0.26.3", {"center": v(80.19, -38.31) * mm, "radius": 2.5 * mm});
            skCircle(sketch, "E17.0.26.4", {"center": v(80.19, -31.31) * mm, "radius": 2.5 * mm});
            skCircle(sketch, "E17.0.26.5", {"center": v(80.19, -24.31) * mm, "radius": 2.5 * mm});
            skCircle(sketch, "E17.0.26.6", {"center": v(80.19, -17.31) * mm, "radius": 2.5 * mm});
            skCircle(sketch, "E17.0.26.7", {"center": v(80.19, -10.31) * mm, "radius": 2.5 * mm});
            skCircle(sketch, "E17.0.26.8", {"center": v(80.19, -3.31) * mm, "radius": 2.5 * mm});
            skCircle(sketch, "E17.0.26.9", {"center": v(80.19, 3.69) * mm, "radius": 2.5 * mm});
            skCircle(sketch, "E17.0.26.10", {"center": v(80.19, 10.69) * mm, "radius": 2.5 * mm});
            skCircle(sketch, "E17.0.26.11", {"center": v(80.19, 17.69) * mm, "radius": 2.5 * mm});
            skCircle(sketch, "E17.0.27.0", {"center": v(87.19, -59.31) * mm, "radius": 2.5 * mm});
            skCircle(sketch, "E17.0.27.1", {"center": v(87.19, -52.31) * mm, "radius": 2.5 * mm});
            skCircle(sketch, "E17.0.27.2", {"center": v(87.19, -45.31) * mm, "radius": 2.5 * mm});
            skCircle(sketch, "E17.0.27.3", {"center": v(87.19, -38.31) * mm, "radius": 2.5 * mm});
            skCircle(sketch, "E17.0.27.4", {"center": v(87.19, -31.31) * mm, "radius": 2.5 * mm});
            skCircle(sketch, "E17.0.27.5", {"center": v(87.19, -24.31) * mm, "radius": 2.5 * mm});
            skCircle(sketch, "E17.0.27.6", {"center": v(87.19, -17.31) * mm, "radius": 2.5 * mm});
            skCircle(sketch, "E17.0.27.7", {"center": v(87.19, -10.31) * mm, "radius": 2.5 * mm});
            skCircle(sketch, "E17.0.27.8", {"center": v(87.19, -3.31) * mm, "radius": 2.5 * mm});
            skCircle(sketch, "E17.0.27.9", {"center": v(87.19, 3.69) * mm, "radius": 2.5 * mm});
            skCircle(sketch, "E17.0.27.10", {"center": v(87.19, 10.69) * mm, "radius": 2.5 * mm});
            skCircle(sketch, "E17.0.27.11", {"center": v(87.19, 17.69) * mm, "radius": 2.5 * mm});
            skCircle(sketch, "E17.0.28.0", {"center": v(94.19, -59.31) * mm, "radius": 2.5 * mm});
            skCircle(sketch, "E17.0.28.1", {"center": v(94.19, -52.31) * mm, "radius": 2.5 * mm});
            skCircle(sketch, "E17.0.28.2", {"center": v(94.19, -45.31) * mm, "radius": 2.5 * mm});
            skCircle(sketch, "E17.0.28.3", {"center": v(94.19, -38.31) * mm, "radius": 2.5 * mm});
            skCircle(sketch, "E17.0.28.4", {"center": v(94.19, -31.31) * mm, "radius": 2.5 * mm});
            skCircle(sketch, "E17.0.28.5", {"center": v(94.19, -24.31) * mm, "radius": 2.5 * mm});
            skCircle(sketch, "E17.0.28.6", {"center": v(94.19, -17.31) * mm, "radius": 2.5 * mm});
            skCircle(sketch, "E17.0.28.7", {"center": v(94.19, -10.31) * mm, "radius": 2.5 * mm});
            skCircle(sketch, "E17.0.28.8", {"center": v(94.19, -3.31) * mm, "radius": 2.5 * mm});
            skCircle(sketch, "E17.0.28.9", {"center": v(94.19, 3.69) * mm, "radius": 2.5 * mm});
            skCircle(sketch, "E17.0.28.10", {"center": v(94.19, 10.69) * mm, "radius": 2.5 * mm});
            skCircle(sketch, "E17.0.28.11", {"center": v(94.19, 17.69) * mm, "radius": 2.5 * mm});
            skCircle(sketch, "E17.0.29.0", {"center": v(101.19, -59.31) * mm, "radius": 2.5 * mm});
            skCircle(sketch, "E17.0.29.1", {"center": v(101.19, -52.31) * mm, "radius": 2.5 * mm});
            skCircle(sketch, "E17.0.29.2", {"center": v(101.19, -45.31) * mm, "radius": 2.5 * mm});
            skCircle(sketch, "E17.0.29.3", {"center": v(101.19, -38.31) * mm, "radius": 2.5 * mm});
            skCircle(sketch, "E17.0.29.4", {"center": v(101.19, -31.31) * mm, "radius": 2.5 * mm});
            skCircle(sketch, "E17.0.29.5", {"center": v(101.19, -24.31) * mm, "radius": 2.5 * mm});
            skCircle(sketch, "E17.0.29.6", {"center": v(101.19, -17.31) * mm, "radius": 2.5 * mm});
            skCircle(sketch, "E17.0.29.7", {"center": v(101.19, -10.31) * mm, "radius": 2.5 * mm});
            skCircle(sketch, "E17.0.29.8", {"center": v(101.19, -3.31) * mm, "radius": 2.5 * mm});
            skCircle(sketch, "E17.0.29.9", {"center": v(101.19, 3.69) * mm, "radius": 2.5 * mm});
            skCircle(sketch, "E17.0.29.10", {"center": v(101.19, 10.69) * mm, "radius": 2.5 * mm});
            skCircle(sketch, "E17.0.29.11", {"center": v(101.19, 17.69) * mm, "radius": 2.5 * mm});
            skCircle(sketch, "E18.0.0.12", {"center": v(-101.81, 24.69) * mm, "radius": 2.5 * mm});
            skCircle(sketch, "E18.0.0.13", {"center": v(-101.81, 31.69) * mm, "radius": 2.5 * mm});
            skCircle(sketch, "E18.0.0.14", {"center": v(-101.81, 38.69) * mm, "radius": 2.5 * mm});
            skCircle(sketch, "E18.0.0.15", {"center": v(-101.81, 45.69) * mm, "radius": 2.5 * mm});
            skCircle(sketch, "E18.0.0.16", {"center": v(-101.81, 52.69) * mm, "radius": 2.5 * mm});
            skCircle(sketch, "E18.0.0.17", {"center": v(-101.81, 59.69) * mm, "radius": 2.5 * mm});
            skCircle(sketch, "E18.0.1.12", {"center": v(-94.81, 24.69) * mm, "radius": 2.5 * mm});
            skCircle(sketch, "E18.0.1.13", {"center": v(-94.81, 31.69) * mm, "radius": 2.5 * mm});
            skCircle(sketch, "E18.0.1.14", {"center": v(-94.81, 38.69) * mm, "radius": 2.5 * mm});
            skCircle(sketch, "E18.0.1.15", {"center": v(-94.81, 45.69) * mm, "radius": 2.5 * mm});
            skCircle(sketch, "E18.0.1.16", {"center": v(-94.81, 52.69) * mm, "radius": 2.5 * mm});
            skCircle(sketch, "E18.0.1.17", {"center": v(-94.81, 59.69) * mm, "radius": 2.5 * mm});
            skCircle(sketch, "E18.0.2.12", {"center": v(-87.81, 24.69) * mm, "radius": 2.5 * mm});
            skCircle(sketch, "E18.0.2.13", {"center": v(-87.81, 31.69) * mm, "radius": 2.5 * mm});
            skCircle(sketch, "E18.0.2.14", {"center": v(-87.81, 38.69) * mm, "radius": 2.5 * mm});
            skCircle(sketch, "E18.0.2.15", {"center": v(-87.81, 45.69) * mm, "radius": 2.5 * mm});
            skCircle(sketch, "E18.0.2.16", {"center": v(-87.81, 52.69) * mm, "radius": 2.5 * mm});
            skCircle(sketch, "E18.0.2.17", {"center": v(-87.81, 59.69) * mm, "radius": 2.5 * mm});
            skCircle(sketch, "E18.0.3.12", {"center": v(-80.81, 24.69) * mm, "radius": 2.5 * mm});
            skCircle(sketch, "E18.0.3.13", {"center": v(-80.81, 31.69) * mm, "radius": 2.5 * mm});
            skCircle(sketch, "E18.0.3.14", {"center": v(-80.81, 38.69) * mm, "radius": 2.5 * mm});
            skCircle(sketch, "E18.0.3.15", {"center": v(-80.81, 45.69) * mm, "radius": 2.5 * mm});
            skCircle(sketch, "E18.0.3.16", {"center": v(-80.81, 52.69) * mm, "radius": 2.5 * mm});
            skCircle(sketch, "E18.0.3.17", {"center": v(-80.81, 59.69) * mm, "radius": 2.5 * mm});
            skCircle(sketch, "E18.0.4.12", {"center": v(-73.81, 24.69) * mm, "radius": 2.5 * mm});
            skCircle(sketch, "E18.0.4.13", {"center": v(-73.81, 31.69) * mm, "radius": 2.5 * mm});
            skCircle(sketch, "E18.0.4.14", {"center": v(-73.81, 38.69) * mm, "radius": 2.5 * mm});
            skCircle(sketch, "E18.0.4.15", {"center": v(-73.81, 45.69) * mm, "radius": 2.5 * mm});
            skCircle(sketch, "E18.0.4.16", {"center": v(-73.81, 52.69) * mm, "radius": 2.5 * mm});
            skCircle(sketch, "E18.0.4.17", {"center": v(-73.81, 59.69) * mm, "radius": 2.5 * mm});
            skCircle(sketch, "E18.0.5.12", {"center": v(-66.81, 24.69) * mm, "radius": 2.5 * mm});
            skCircle(sketch, "E18.0.5.13", {"center": v(-66.81, 31.69) * mm, "radius": 2.5 * mm});
            skCircle(sketch, "E18.0.5.14", {"center": v(-66.81, 38.69) * mm, "radius": 2.5 * mm});
            skCircle(sketch, "E18.0.5.15", {"center": v(-66.81, 45.69) * mm, "radius": 2.5 * mm});
            skCircle(sketch, "E18.0.5.16", {"center": v(-66.81, 52.69) * mm, "radius": 2.5 * mm});
            skCircle(sketch, "E18.0.5.17", {"center": v(-66.81, 59.69) * mm, "radius": 2.5 * mm});
            skCircle(sketch, "E18.0.6.12", {"center": v(-59.81, 24.69) * mm, "radius": 2.5 * mm});
            skCircle(sketch, "E18.0.6.13", {"center": v(-59.81, 31.69) * mm, "radius": 2.5 * mm});
            skCircle(sketch, "E18.0.6.14", {"center": v(-59.81, 38.69) * mm, "radius": 2.5 * mm});
            skCircle(sketch, "E18.0.6.15", {"center": v(-59.81, 45.69) * mm, "radius": 2.5 * mm});
            skCircle(sketch, "E18.0.6.16", {"center": v(-59.81, 52.69) * mm, "radius": 2.5 * mm});
            skCircle(sketch, "E18.0.6.17", {"center": v(-59.81, 59.69) * mm, "radius": 2.5 * mm});
            skCircle(sketch, "E18.0.7.12", {"center": v(-52.81, 24.69) * mm, "radius": 2.5 * mm});
            skCircle(sketch, "E18.0.7.13", {"center": v(-52.81, 31.69) * mm, "radius": 2.5 * mm});
            skCircle(sketch, "E18.0.7.14", {"center": v(-52.81, 38.69) * mm, "radius": 2.5 * mm});
            skCircle(sketch, "E18.0.7.15", {"center": v(-52.81, 45.69) * mm, "radius": 2.5 * mm});
            skCircle(sketch, "E18.0.7.16", {"center": v(-52.81, 52.69) * mm, "radius": 2.5 * mm});
            skCircle(sketch, "E18.0.7.17", {"center": v(-52.81, 59.69) * mm, "radius": 2.5 * mm});
            skCircle(sketch, "E18.0.8.12", {"center": v(-45.81, 24.69) * mm, "radius": 2.5 * mm});
            skCircle(sketch, "E18.0.8.13", {"center": v(-45.81, 31.69) * mm, "radius": 2.5 * mm});
            skCircle(sketch, "E18.0.8.14", {"center": v(-45.81, 38.69) * mm, "radius": 2.5 * mm});
            skCircle(sketch, "E18.0.8.15", {"center": v(-45.81, 45.69) * mm, "radius": 2.5 * mm});
            skCircle(sketch, "E18.0.8.16", {"center": v(-45.81, 52.69) * mm, "radius": 2.5 * mm});
            skCircle(sketch, "E18.0.8.17", {"center": v(-45.81, 59.69) * mm, "radius": 2.5 * mm});
            skCircle(sketch, "E18.0.9.12", {"center": v(-38.81, 24.69) * mm, "radius": 2.5 * mm});
            skCircle(sketch, "E18.0.9.13", {"center": v(-38.81, 31.69) * mm, "radius": 2.5 * mm});
            skCircle(sketch, "E18.0.9.14", {"center": v(-38.81, 38.69) * mm, "radius": 2.5 * mm});
            skCircle(sketch, "E18.0.9.15", {"center": v(-38.81, 45.69) * mm, "radius": 2.5 * mm});
            skCircle(sketch, "E18.0.9.16", {"center": v(-38.81, 52.69) * mm, "radius": 2.5 * mm});
            skCircle(sketch, "E18.0.9.17", {"center": v(-38.81, 59.69) * mm, "radius": 2.5 * mm});
            skCircle(sketch, "E18.0.10.12", {"center": v(-31.81, 24.69) * mm, "radius": 2.5 * mm});
            skCircle(sketch, "E18.0.10.13", {"center": v(-31.81, 31.69) * mm, "radius": 2.5 * mm});
            skCircle(sketch, "E18.0.10.14", {"center": v(-31.81, 38.69) * mm, "radius": 2.5 * mm});
            skCircle(sketch, "E18.0.10.15", {"center": v(-31.81, 45.69) * mm, "radius": 2.5 * mm});
            skCircle(sketch, "E18.0.10.16", {"center": v(-31.81, 52.69) * mm, "radius": 2.5 * mm});
            skCircle(sketch, "E18.0.10.17", {"center": v(-31.81, 59.69) * mm, "radius": 2.5 * mm});
            skCircle(sketch, "E18.0.11.12", {"center": v(-24.81, 24.69) * mm, "radius": 2.5 * mm});
            skCircle(sketch, "E18.0.11.13", {"center": v(-24.81, 31.69) * mm, "radius": 2.5 * mm});
            skCircle(sketch, "E18.0.11.14", {"center": v(-24.81, 38.69) * mm, "radius": 2.5 * mm});
            skCircle(sketch, "E18.0.11.15", {"center": v(-24.81, 45.69) * mm, "radius": 2.5 * mm});
            skCircle(sketch, "E18.0.11.16", {"center": v(-24.81, 52.69) * mm, "radius": 2.5 * mm});
            skCircle(sketch, "E18.0.11.17", {"center": v(-24.81, 59.69) * mm, "radius": 2.5 * mm});
            skCircle(sketch, "E18.0.12.12", {"center": v(-17.81, 24.69) * mm, "radius": 2.5 * mm});
            skCircle(sketch, "E18.0.12.13", {"center": v(-17.81, 31.69) * mm, "radius": 2.5 * mm});
            skCircle(sketch, "E18.0.12.14", {"center": v(-17.81, 38.69) * mm, "radius": 2.5 * mm});
            skCircle(sketch, "E18.0.12.15", {"center": v(-17.81, 45.69) * mm, "radius": 2.5 * mm});
            skCircle(sketch, "E18.0.12.16", {"center": v(-17.81, 52.69) * mm, "radius": 2.5 * mm});
            skCircle(sketch, "E18.0.12.17", {"center": v(-17.81, 59.69) * mm, "radius": 2.5 * mm});
            skCircle(sketch, "E18.0.13.12", {"center": v(-10.81, 24.69) * mm, "radius": 2.5 * mm});
            skCircle(sketch, "E18.0.13.13", {"center": v(-10.81, 31.69) * mm, "radius": 2.5 * mm});
            skCircle(sketch, "E18.0.13.14", {"center": v(-10.81, 38.69) * mm, "radius": 2.5 * mm});
            skCircle(sketch, "E18.0.13.15", {"center": v(-10.81, 45.69) * mm, "radius": 2.5 * mm});
            skCircle(sketch, "E18.0.13.16", {"center": v(-10.81, 52.69) * mm, "radius": 2.5 * mm});
            skCircle(sketch, "E18.0.13.17", {"center": v(-10.81, 59.69) * mm, "radius": 2.5 * mm});
            skCircle(sketch, "E18.0.14.12", {"center": v(-3.81, 24.69) * mm, "radius": 2.5 * mm});
            skCircle(sketch, "E18.0.14.13", {"center": v(-3.81, 31.69) * mm, "radius": 2.5 * mm});
            skCircle(sketch, "E18.0.14.14", {"center": v(-3.81, 38.69) * mm, "radius": 2.5 * mm});
            skCircle(sketch, "E18.0.14.15", {"center": v(-3.81, 45.69) * mm, "radius": 2.5 * mm});
            skCircle(sketch, "E18.0.14.16", {"center": v(-3.81, 52.69) * mm, "radius": 2.5 * mm});
            skCircle(sketch, "E18.0.14.17", {"center": v(-3.81, 59.69) * mm, "radius": 2.5 * mm});
            skCircle(sketch, "E18.0.15.12", {"center": v(3.19, 24.69) * mm, "radius": 2.5 * mm});
            skCircle(sketch, "E18.0.15.13", {"center": v(3.19, 31.69) * mm, "radius": 2.5 * mm});
            skCircle(sketch, "E18.0.15.14", {"center": v(3.19, 38.69) * mm, "radius": 2.5 * mm});
            skCircle(sketch, "E18.0.15.15", {"center": v(3.19, 45.69) * mm, "radius": 2.5 * mm});
            skCircle(sketch, "E18.0.15.16", {"center": v(3.19, 52.69) * mm, "radius": 2.5 * mm});
            skCircle(sketch, "E18.0.15.17", {"center": v(3.19, 59.69) * mm, "radius": 2.5 * mm});
            skCircle(sketch, "E18.0.16.12", {"center": v(10.19, 24.69) * mm, "radius": 2.5 * mm});
            skCircle(sketch, "E18.0.16.13", {"center": v(10.19, 31.69) * mm, "radius": 2.5 * mm});
            skCircle(sketch, "E18.0.16.14", {"center": v(10.19, 38.69) * mm, "radius": 2.5 * mm});
            skCircle(sketch, "E18.0.16.15", {"center": v(10.19, 45.69) * mm, "radius": 2.5 * mm});
            skCircle(sketch, "E18.0.16.16", {"center": v(10.19, 52.69) * mm, "radius": 2.5 * mm});
            skCircle(sketch, "E18.0.16.17", {"center": v(10.19, 59.69) * mm, "radius": 2.5 * mm});
            skCircle(sketch, "E18.0.17.12", {"center": v(17.19, 24.69) * mm, "radius": 2.5 * mm});
            skCircle(sketch, "E18.0.17.13", {"center": v(17.19, 31.69) * mm, "radius": 2.5 * mm});
            skCircle(sketch, "E18.0.17.14", {"center": v(17.19, 38.69) * mm, "radius": 2.5 * mm});
            skCircle(sketch, "E18.0.17.15", {"center": v(17.19, 45.69) * mm, "radius": 2.5 * mm});
            skCircle(sketch, "E18.0.17.16", {"center": v(17.19, 52.69) * mm, "radius": 2.5 * mm});
            skCircle(sketch, "E18.0.17.17", {"center": v(17.19, 59.69) * mm, "radius": 2.5 * mm});
            skCircle(sketch, "E18.0.18.12", {"center": v(24.19, 24.69) * mm, "radius": 2.5 * mm});
            skCircle(sketch, "E18.0.18.13", {"center": v(24.19, 31.69) * mm, "radius": 2.5 * mm});
            skCircle(sketch, "E18.0.18.14", {"center": v(24.19, 38.69) * mm, "radius": 2.5 * mm});
            skCircle(sketch, "E18.0.18.15", {"center": v(24.19, 45.69) * mm, "radius": 2.5 * mm});
            skCircle(sketch, "E18.0.18.16", {"center": v(24.19, 52.69) * mm, "radius": 2.5 * mm});
            skCircle(sketch, "E18.0.18.17", {"center": v(24.19, 59.69) * mm, "radius": 2.5 * mm});
            skCircle(sketch, "E18.0.19.12", {"center": v(31.19, 24.69) * mm, "radius": 2.5 * mm});
            skCircle(sketch, "E18.0.19.13", {"center": v(31.19, 31.69) * mm, "radius": 2.5 * mm});
            skCircle(sketch, "E18.0.19.14", {"center": v(31.19, 38.69) * mm, "radius": 2.5 * mm});
            skCircle(sketch, "E18.0.19.15", {"center": v(31.19, 45.69) * mm, "radius": 2.5 * mm});
            skCircle(sketch, "E18.0.19.16", {"center": v(31.19, 52.69) * mm, "radius": 2.5 * mm});
            skCircle(sketch, "E18.0.19.17", {"center": v(31.19, 59.69) * mm, "radius": 2.5 * mm});
            skCircle(sketch, "E18.0.20.12", {"center": v(38.19, 24.69) * mm, "radius": 2.5 * mm});
            skCircle(sketch, "E18.0.20.13", {"center": v(38.19, 31.69) * mm, "radius": 2.5 * mm});
            skCircle(sketch, "E18.0.20.14", {"center": v(38.19, 38.69) * mm, "radius": 2.5 * mm});
            skCircle(sketch, "E18.0.20.15", {"center": v(38.19, 45.69) * mm, "radius": 2.5 * mm});
            skCircle(sketch, "E18.0.20.16", {"center": v(38.19, 52.69) * mm, "radius": 2.5 * mm});
            skCircle(sketch, "E18.0.20.17", {"center": v(38.19, 59.69) * mm, "radius": 2.5 * mm});
            skCircle(sketch, "E18.0.21.12", {"center": v(45.19, 24.69) * mm, "radius": 2.5 * mm});
            skCircle(sketch, "E18.0.21.13", {"center": v(45.19, 31.69) * mm, "radius": 2.5 * mm});
            skCircle(sketch, "E18.0.21.14", {"center": v(45.19, 38.69) * mm, "radius": 2.5 * mm});
            skCircle(sketch, "E18.0.21.15", {"center": v(45.19, 45.69) * mm, "radius": 2.5 * mm});
            skCircle(sketch, "E18.0.21.16", {"center": v(45.19, 52.69) * mm, "radius": 2.5 * mm});
            skCircle(sketch, "E18.0.21.17", {"center": v(45.19, 59.69) * mm, "radius": 2.5 * mm});
            skCircle(sketch, "E18.0.22.12", {"center": v(52.19, 24.69) * mm, "radius": 2.5 * mm});
            skCircle(sketch, "E18.0.22.13", {"center": v(52.19, 31.69) * mm, "radius": 2.5 * mm});
            skCircle(sketch, "E18.0.22.14", {"center": v(52.19, 38.69) * mm, "radius": 2.5 * mm});
            skCircle(sketch, "E18.0.22.15", {"center": v(52.19, 45.69) * mm, "radius": 2.5 * mm});
            skCircle(sketch, "E18.0.22.16", {"center": v(52.19, 52.69) * mm, "radius": 2.5 * mm});
            skCircle(sketch, "E18.0.22.17", {"center": v(52.19, 59.69) * mm, "radius": 2.5 * mm});
            skCircle(sketch, "E18.0.23.12", {"center": v(59.19, 24.69) * mm, "radius": 2.5 * mm});
            skCircle(sketch, "E18.0.23.13", {"center": v(59.19, 31.69) * mm, "radius": 2.5 * mm});
            skCircle(sketch, "E18.0.23.14", {"center": v(59.19, 38.69) * mm, "radius": 2.5 * mm});
            skCircle(sketch, "E18.0.23.15", {"center": v(59.19, 45.69) * mm, "radius": 2.5 * mm});
            skCircle(sketch, "E18.0.23.16", {"center": v(59.19, 52.69) * mm, "radius": 2.5 * mm});
            skCircle(sketch, "E18.0.23.17", {"center": v(59.19, 59.69) * mm, "radius": 2.5 * mm});
            skCircle(sketch, "E18.0.24.12", {"center": v(66.19, 24.69) * mm, "radius": 2.5 * mm});
            skCircle(sketch, "E18.0.24.13", {"center": v(66.19, 31.69) * mm, "radius": 2.5 * mm});
            skCircle(sketch, "E18.0.24.14", {"center": v(66.19, 38.69) * mm, "radius": 2.5 * mm});
            skCircle(sketch, "E18.0.24.15", {"center": v(66.19, 45.69) * mm, "radius": 2.5 * mm});
            skCircle(sketch, "E18.0.24.16", {"center": v(66.19, 52.69) * mm, "radius": 2.5 * mm});
            skCircle(sketch, "E18.0.24.17", {"center": v(66.19, 59.69) * mm, "radius": 2.5 * mm});
            skCircle(sketch, "E18.0.25.12", {"center": v(73.19, 24.69) * mm, "radius": 2.5 * mm});
            skCircle(sketch, "E18.0.25.13", {"center": v(73.19, 31.69) * mm, "radius": 2.5 * mm});
            skCircle(sketch, "E18.0.25.14", {"center": v(73.19, 38.69) * mm, "radius": 2.5 * mm});
            skCircle(sketch, "E18.0.25.15", {"center": v(73.19, 45.69) * mm, "radius": 2.5 * mm});
            skCircle(sketch, "E18.0.25.16", {"center": v(73.19, 52.69) * mm, "radius": 2.5 * mm});
            skCircle(sketch, "E18.0.25.17", {"center": v(73.19, 59.69) * mm, "radius": 2.5 * mm});
            skCircle(sketch, "E18.0.26.12", {"center": v(80.19, 24.69) * mm, "radius": 2.5 * mm});
            skCircle(sketch, "E18.0.26.13", {"center": v(80.19, 31.69) * mm, "radius": 2.5 * mm});
            skCircle(sketch, "E18.0.26.14", {"center": v(80.19, 38.69) * mm, "radius": 2.5 * mm});
            skCircle(sketch, "E18.0.26.15", {"center": v(80.19, 45.69) * mm, "radius": 2.5 * mm});
            skCircle(sketch, "E18.0.26.16", {"center": v(80.19, 52.69) * mm, "radius": 2.5 * mm});
            skCircle(sketch, "E18.0.26.17", {"center": v(80.19, 59.69) * mm, "radius": 2.5 * mm});
            skCircle(sketch, "E18.0.27.12", {"center": v(87.19, 24.69) * mm, "radius": 2.5 * mm});
            skCircle(sketch, "E18.0.27.13", {"center": v(87.19, 31.69) * mm, "radius": 2.5 * mm});
            skCircle(sketch, "E18.0.27.14", {"center": v(87.19, 38.69) * mm, "radius": 2.5 * mm});
            skCircle(sketch, "E18.0.27.15", {"center": v(87.19, 45.69) * mm, "radius": 2.5 * mm});
            skCircle(sketch, "E18.0.27.16", {"center": v(87.19, 52.69) * mm, "radius": 2.5 * mm});
            skCircle(sketch, "E18.0.27.17", {"center": v(87.19, 59.69) * mm, "radius": 2.5 * mm});
            skCircle(sketch, "E18.0.28.12", {"center": v(94.19, 24.69) * mm, "radius": 2.5 * mm});
            skCircle(sketch, "E18.0.28.13", {"center": v(94.19, 31.69) * mm, "radius": 2.5 * mm});
            skCircle(sketch, "E18.0.28.14", {"center": v(94.19, 38.69) * mm, "radius": 2.5 * mm});
            skCircle(sketch, "E18.0.28.15", {"center": v(94.19, 45.69) * mm, "radius": 2.5 * mm});
            skCircle(sketch, "E18.0.28.16", {"center": v(94.19, 52.69) * mm, "radius": 2.5 * mm});
            skCircle(sketch, "E18.0.28.17", {"center": v(94.19, 59.69) * mm, "radius": 2.5 * mm});
            skCircle(sketch, "E18.0.29.12", {"center": v(101.19, 24.69) * mm, "radius": 2.5 * mm});
            skCircle(sketch, "E18.0.29.13", {"center": v(101.19, 31.69) * mm, "radius": 2.5 * mm});
            skCircle(sketch, "E18.0.29.14", {"center": v(101.19, 38.69) * mm, "radius": 2.5 * mm});
            skCircle(sketch, "E18.0.29.15", {"center": v(101.19, 45.69) * mm, "radius": 2.5 * mm});
            skCircle(sketch, "E18.0.29.16", {"center": v(101.19, 52.69) * mm, "radius": 2.5 * mm});
            skCircle(sketch, "E18.0.29.17", {"center": v(101.19, 59.69) * mm, "radius": 2.5 * mm});
            skSolve(sketch);
        }
        {
            var Q0;
            Q0 = qSketchRegion(id + "F10", true);
            extrude(context, id + "F11", {"entities" : qUnion([Q0]), "operationType" : NewBodyOperationType.REMOVE, "oppositeDirection" : true, "depth" : (getVariable(context, 'thickness')), "offsetDistance" : 25 * mm});
        }
        {
            var Q0;
            Q0=qCreatedBy(makeId("Right.planeOp"),FACE);
            var sketch = newSketch(context, id + "F12", { "sketchPlane" : qUnion([Q0])});
            skLineSegment(sketch, "E19.bottom", {"start": v(-62.06, 43.02) * mm, "end": v(-58.53, 39.49) * mm});
            skLineSegment(sketch, "E19.top", {"start": v(-65.6, 39.49) * mm, "end": v(-62.06, 35.95) * mm});
            skLineSegment(sketch, "E19.left", {"start": v(-62.06, 43.02) * mm, "end": v(-65.6, 39.49) * mm});
            skLineSegment(sketch, "E19.right", {"start": v(-58.53, 39.49) * mm, "end": v(-62.06, 35.95) * mm});
            skLineSegment(sketch, "E20.bottom", {"start": v(-57.11, 38.07) * mm, "end": v(-53.58, 34.54) * mm});
            skLineSegment(sketch, "E20.top", {"start": v(-60.65, 34.54) * mm, "end": v(-57.11, 31) * mm});
            skLineSegment(sketch, "E20.left", {"start": v(-57.11, 38.07) * mm, "end": v(-60.65, 34.54) * mm});
            skLineSegment(sketch, "E20.right", {"start": v(-53.58, 34.54) * mm, "end": v(-57.11, 31) * mm});
            skLineSegment(sketch, "E21", {"start": v(-62.06, 35.95) * mm, "end": v(-60.65, 34.54) * mm});
            skLineSegment(sketch, "E22.0.1.0", {"start": v(-53.58, 24.54) * mm, "end": v(-57.11, 21) * mm});
            skLineSegment(sketch, "E22.0.1.1", {"start": v(-57.11, 28.07) * mm, "end": v(-53.58, 24.54) * mm});
            skLineSegment(sketch, "E22.0.1.2", {"start": v(-62.06, 33.02) * mm, "end": v(-65.6, 29.49) * mm});
            skLineSegment(sketch, "E22.0.1.3", {"start": v(-62.06, 33.02) * mm, "end": v(-58.53, 29.49) * mm});
            skLineSegment(sketch, "E22.0.1.4", {"start": v(-57.11, 28.07) * mm, "end": v(-60.65, 24.54) * mm});
            skLineSegment(sketch, "E22.0.1.5", {"start": v(-62.06, 25.95) * mm, "end": v(-60.65, 24.54) * mm});
            skLineSegment(sketch, "E22.0.1.6", {"start": v(-60.65, 24.54) * mm, "end": v(-57.11, 21) * mm});
            skLineSegment(sketch, "E22.0.1.7", {"start": v(-58.53, 29.49) * mm, "end": v(-62.06, 25.95) * mm});
            skLineSegment(sketch, "E22.0.1.8", {"start": v(-65.6, 29.49) * mm, "end": v(-62.06, 25.95) * mm});
            skLineSegment(sketch, "E22.0.2.0", {"start": v(-53.58, 14.54) * mm, "end": v(-57.11, 11) * mm});
            skLineSegment(sketch, "E22.0.2.1", {"start": v(-57.11, 18.07) * mm, "end": v(-53.58, 14.54) * mm});
            skLineSegment(sketch, "E22.0.2.2", {"start": v(-62.06, 23.02) * mm, "end": v(-65.6, 19.49) * mm});
            skLineSegment(sketch, "E22.0.2.3", {"start": v(-62.06, 23.02) * mm, "end": v(-58.53, 19.49) * mm});
            skLineSegment(sketch, "E22.0.2.4", {"start": v(-57.11, 18.07) * mm, "end": v(-60.65, 14.54) * mm});
            skLineSegment(sketch, "E22.0.2.5", {"start": v(-62.06, 15.95) * mm, "end": v(-60.65, 14.54) * mm});
            skLineSegment(sketch, "E22.0.2.6", {"start": v(-60.65, 14.54) * mm, "end": v(-57.11, 11) * mm});
            skLineSegment(sketch, "E22.0.2.7", {"start": v(-58.53, 19.49) * mm, "end": v(-62.06, 15.95) * mm});
            skLineSegment(sketch, "E22.0.2.8", {"start": v(-65.6, 19.49) * mm, "end": v(-62.06, 15.95) * mm});
            skLineSegment(sketch, "E22.0.3.0", {"start": v(-53.58, 4.54) * mm, "end": v(-57.11, 1) * mm});
            skLineSegment(sketch, "E22.0.3.1", {"start": v(-57.11, 8.07) * mm, "end": v(-53.58, 4.54) * mm});
            skLineSegment(sketch, "E22.0.3.2", {"start": v(-62.06, 13.02) * mm, "end": v(-65.6, 9.49) * mm});
            skLineSegment(sketch, "E22.0.3.3", {"start": v(-62.06, 13.02) * mm, "end": v(-58.53, 9.49) * mm});
            skLineSegment(sketch, "E22.0.3.4", {"start": v(-57.11, 8.07) * mm, "end": v(-60.65, 4.54) * mm});
            skLineSegment(sketch, "E22.0.3.5", {"start": v(-62.06, 5.95) * mm, "end": v(-60.65, 4.54) * mm});
            skLineSegment(sketch, "E22.0.3.6", {"start": v(-60.65, 4.54) * mm, "end": v(-57.11, 1) * mm});
            skLineSegment(sketch, "E22.0.3.7", {"start": v(-58.53, 9.49) * mm, "end": v(-62.06, 5.95) * mm});
            skLineSegment(sketch, "E22.0.3.8", {"start": v(-65.6, 9.49) * mm, "end": v(-62.06, 5.95) * mm});
            skLineSegment(sketch, "E22.1.0.0", {"start": v(-43.58, 34.54) * mm, "end": v(-47.11, 31) * mm});
            skLineSegment(sketch, "E22.1.0.1", {"start": v(-47.11, 38.07) * mm, "end": v(-43.58, 34.54) * mm});
            skLineSegment(sketch, "E22.1.0.2", {"start": v(-52.06, 43.02) * mm, "end": v(-55.6, 39.49) * mm});
            skLineSegment(sketch, "E22.1.0.3", {"start": v(-52.06, 43.02) * mm, "end": v(-48.53, 39.49) * mm});
            skLineSegment(sketch, "E22.1.0.4", {"start": v(-47.11, 38.07) * mm, "end": v(-50.65, 34.54) * mm});
            skLineSegment(sketch, "E22.1.0.5", {"start": v(-52.06, 35.95) * mm, "end": v(-50.65, 34.54) * mm});
            skLineSegment(sketch, "E22.1.0.6", {"start": v(-50.65, 34.54) * mm, "end": v(-47.11, 31) * mm});
            skLineSegment(sketch, "E22.1.0.7", {"start": v(-48.53, 39.49) * mm, "end": v(-52.06, 35.95) * mm});
            skLineSegment(sketch, "E22.1.0.8", {"start": v(-55.6, 39.49) * mm, "end": v(-52.06, 35.95) * mm});
            skLineSegment(sketch, "E22.1.1.0", {"start": v(-43.58, 24.54) * mm, "end": v(-47.11, 21) * mm});
            skLineSegment(sketch, "E22.1.1.1", {"start": v(-47.11, 28.07) * mm, "end": v(-43.58, 24.54) * mm});
            skLineSegment(sketch, "E22.1.1.2", {"start": v(-52.06, 33.02) * mm, "end": v(-55.6, 29.49) * mm});
            skLineSegment(sketch, "E22.1.1.3", {"start": v(-52.06, 33.02) * mm, "end": v(-48.53, 29.49) * mm});
            skLineSegment(sketch, "E22.1.1.4", {"start": v(-47.11, 28.07) * mm, "end": v(-50.65, 24.54) * mm});
            skLineSegment(sketch, "E22.1.1.5", {"start": v(-52.06, 25.95) * mm, "end": v(-50.65, 24.54) * mm});
            skLineSegment(sketch, "E22.1.1.6", {"start": v(-50.65, 24.54) * mm, "end": v(-47.11, 21) * mm});
            skLineSegment(sketch, "E22.1.1.7", {"start": v(-48.53, 29.49) * mm, "end": v(-52.06, 25.95) * mm});
            skLineSegment(sketch, "E22.1.1.8", {"start": v(-55.6, 29.49) * mm, "end": v(-52.06, 25.95) * mm});
            skLineSegment(sketch, "E22.1.2.0", {"start": v(-43.58, 14.54) * mm, "end": v(-47.11, 11) * mm});
            skLineSegment(sketch, "E22.1.2.1", {"start": v(-47.11, 18.07) * mm, "end": v(-43.58, 14.54) * mm});
            skLineSegment(sketch, "E22.1.2.2", {"start": v(-52.06, 23.02) * mm, "end": v(-55.6, 19.49) * mm});
            skLineSegment(sketch, "E22.1.2.3", {"start": v(-52.06, 23.02) * mm, "end": v(-48.53, 19.49) * mm});
            skLineSegment(sketch, "E22.1.2.4", {"start": v(-47.11, 18.07) * mm, "end": v(-50.65, 14.54) * mm});
            skLineSegment(sketch, "E22.1.2.5", {"start": v(-52.06, 15.95) * mm, "end": v(-50.65, 14.54) * mm});
            skLineSegment(sketch, "E22.1.2.6", {"start": v(-50.65, 14.54) * mm, "end": v(-47.11, 11) * mm});
            skLineSegment(sketch, "E22.1.2.7", {"start": v(-48.53, 19.49) * mm, "end": v(-52.06, 15.95) * mm});
            skLineSegment(sketch, "E22.1.2.8", {"start": v(-55.6, 19.49) * mm, "end": v(-52.06, 15.95) * mm});
            skLineSegment(sketch, "E22.1.3.0", {"start": v(-43.58, 4.54) * mm, "end": v(-47.11, 1) * mm});
            skLineSegment(sketch, "E22.1.3.1", {"start": v(-47.11, 8.07) * mm, "end": v(-43.58, 4.54) * mm});
            skLineSegment(sketch, "E22.1.3.2", {"start": v(-52.06, 13.02) * mm, "end": v(-55.6, 9.49) * mm});
            skLineSegment(sketch, "E22.1.3.3", {"start": v(-52.06, 13.02) * mm, "end": v(-48.53, 9.49) * mm});
            skLineSegment(sketch, "E22.1.3.4", {"start": v(-47.11, 8.07) * mm, "end": v(-50.65, 4.54) * mm});
            skLineSegment(sketch, "E22.1.3.5", {"start": v(-52.06, 5.95) * mm, "end": v(-50.65, 4.54) * mm});
            skLineSegment(sketch, "E22.1.3.6", {"start": v(-50.65, 4.54) * mm, "end": v(-47.11, 1) * mm});
            skLineSegment(sketch, "E22.1.3.7", {"start": v(-48.53, 9.49) * mm, "end": v(-52.06, 5.95) * mm});
            skLineSegment(sketch, "E22.1.3.8", {"start": v(-55.6, 9.49) * mm, "end": v(-52.06, 5.95) * mm});
            skLineSegment(sketch, "E22.2.0.0", {"start": v(-33.58, 34.54) * mm, "end": v(-37.11, 31) * mm});
            skLineSegment(sketch, "E22.2.0.1", {"start": v(-37.11, 38.07) * mm, "end": v(-33.58, 34.54) * mm});
            skLineSegment(sketch, "E22.2.0.2", {"start": v(-42.06, 43.02) * mm, "end": v(-45.6, 39.49) * mm});
            skLineSegment(sketch, "E22.2.0.3", {"start": v(-42.06, 43.02) * mm, "end": v(-38.53, 39.49) * mm});
            skLineSegment(sketch, "E22.2.0.4", {"start": v(-37.11, 38.07) * mm, "end": v(-40.65, 34.54) * mm});
            skLineSegment(sketch, "E22.2.0.5", {"start": v(-42.06, 35.95) * mm, "end": v(-40.65, 34.54) * mm});
            skLineSegment(sketch, "E22.2.0.6", {"start": v(-40.65, 34.54) * mm, "end": v(-37.11, 31) * mm});
            skLineSegment(sketch, "E22.2.0.7", {"start": v(-38.53, 39.49) * mm, "end": v(-42.06, 35.95) * mm});
            skLineSegment(sketch, "E22.2.0.8", {"start": v(-45.6, 39.49) * mm, "end": v(-42.06, 35.95) * mm});
            skLineSegment(sketch, "E22.2.1.0", {"start": v(-33.58, 24.54) * mm, "end": v(-37.11, 21) * mm});
            skLineSegment(sketch, "E22.2.1.1", {"start": v(-37.11, 28.07) * mm, "end": v(-33.58, 24.54) * mm});
            skLineSegment(sketch, "E22.2.1.2", {"start": v(-42.06, 33.02) * mm, "end": v(-45.6, 29.49) * mm});
            skLineSegment(sketch, "E22.2.1.3", {"start": v(-42.06, 33.02) * mm, "end": v(-38.53, 29.49) * mm});
            skLineSegment(sketch, "E22.2.1.4", {"start": v(-37.11, 28.07) * mm, "end": v(-40.65, 24.54) * mm});
            skLineSegment(sketch, "E22.2.1.5", {"start": v(-42.06, 25.95) * mm, "end": v(-40.65, 24.54) * mm});
            skLineSegment(sketch, "E22.2.1.6", {"start": v(-40.65, 24.54) * mm, "end": v(-37.11, 21) * mm});
            skLineSegment(sketch, "E22.2.1.7", {"start": v(-38.53, 29.49) * mm, "end": v(-42.06, 25.95) * mm});
            skLineSegment(sketch, "E22.2.1.8", {"start": v(-45.6, 29.49) * mm, "end": v(-42.06, 25.95) * mm});
            skLineSegment(sketch, "E22.2.2.0", {"start": v(-33.58, 14.54) * mm, "end": v(-37.11, 11) * mm});
            skLineSegment(sketch, "E22.2.2.1", {"start": v(-37.11, 18.07) * mm, "end": v(-33.58, 14.54) * mm});
            skLineSegment(sketch, "E22.2.2.2", {"start": v(-42.06, 23.02) * mm, "end": v(-45.6, 19.49) * mm});
            skLineSegment(sketch, "E22.2.2.3", {"start": v(-42.06, 23.02) * mm, "end": v(-38.53, 19.49) * mm});
            skLineSegment(sketch, "E22.2.2.4", {"start": v(-37.11, 18.07) * mm, "end": v(-40.65, 14.54) * mm});
            skLineSegment(sketch, "E22.2.2.5", {"start": v(-42.06, 15.95) * mm, "end": v(-40.65, 14.54) * mm});
            skLineSegment(sketch, "E22.2.2.6", {"start": v(-40.65, 14.54) * mm, "end": v(-37.11, 11) * mm});
            skLineSegment(sketch, "E22.2.2.7", {"start": v(-38.53, 19.49) * mm, "end": v(-42.06, 15.95) * mm});
            skLineSegment(sketch, "E22.2.2.8", {"start": v(-45.6, 19.49) * mm, "end": v(-42.06, 15.95) * mm});
            skLineSegment(sketch, "E22.2.3.0", {"start": v(-33.58, 4.54) * mm, "end": v(-37.11, 1) * mm});
            skLineSegment(sketch, "E22.2.3.1", {"start": v(-37.11, 8.07) * mm, "end": v(-33.58, 4.54) * mm});
            skLineSegment(sketch, "E22.2.3.2", {"start": v(-42.06, 13.02) * mm, "end": v(-45.6, 9.49) * mm});
            skLineSegment(sketch, "E22.2.3.3", {"start": v(-42.06, 13.02) * mm, "end": v(-38.53, 9.49) * mm});
            skLineSegment(sketch, "E22.2.3.4", {"start": v(-37.11, 8.07) * mm, "end": v(-40.65, 4.54) * mm});
            skLineSegment(sketch, "E22.2.3.5", {"start": v(-42.06, 5.95) * mm, "end": v(-40.65, 4.54) * mm});
            skLineSegment(sketch, "E22.2.3.6", {"start": v(-40.65, 4.54) * mm, "end": v(-37.11, 1) * mm});
            skLineSegment(sketch, "E22.2.3.7", {"start": v(-38.53, 9.49) * mm, "end": v(-42.06, 5.95) * mm});
            skLineSegment(sketch, "E22.2.3.8", {"start": v(-45.6, 9.49) * mm, "end": v(-42.06, 5.95) * mm});
            skLineSegment(sketch, "E22.3.0.0", {"start": v(-23.58, 34.54) * mm, "end": v(-27.11, 31) * mm});
            skLineSegment(sketch, "E22.3.0.1", {"start": v(-27.11, 38.07) * mm, "end": v(-23.58, 34.54) * mm});
            skLineSegment(sketch, "E22.3.0.2", {"start": v(-32.06, 43.02) * mm, "end": v(-35.6, 39.49) * mm});
            skLineSegment(sketch, "E22.3.0.3", {"start": v(-32.06, 43.02) * mm, "end": v(-28.53, 39.49) * mm});
            skLineSegment(sketch, "E22.3.0.4", {"start": v(-27.11, 38.07) * mm, "end": v(-30.65, 34.54) * mm});
            skLineSegment(sketch, "E22.3.0.5", {"start": v(-32.06, 35.95) * mm, "end": v(-30.65, 34.54) * mm});
            skLineSegment(sketch, "E22.3.0.6", {"start": v(-30.65, 34.54) * mm, "end": v(-27.11, 31) * mm});
            skLineSegment(sketch, "E22.3.0.7", {"start": v(-28.53, 39.49) * mm, "end": v(-32.06, 35.95) * mm});
            skLineSegment(sketch, "E22.3.0.8", {"start": v(-35.6, 39.49) * mm, "end": v(-32.06, 35.95) * mm});
            skLineSegment(sketch, "E22.3.1.0", {"start": v(-23.58, 24.54) * mm, "end": v(-27.11, 21) * mm});
            skLineSegment(sketch, "E22.3.1.1", {"start": v(-27.11, 28.07) * mm, "end": v(-23.58, 24.54) * mm});
            skLineSegment(sketch, "E22.3.1.2", {"start": v(-32.06, 33.02) * mm, "end": v(-35.6, 29.49) * mm});
            skLineSegment(sketch, "E22.3.1.3", {"start": v(-32.06, 33.02) * mm, "end": v(-28.53, 29.49) * mm});
            skLineSegment(sketch, "E22.3.1.4", {"start": v(-27.11, 28.07) * mm, "end": v(-30.65, 24.54) * mm});
            skLineSegment(sketch, "E22.3.1.5", {"start": v(-32.06, 25.95) * mm, "end": v(-30.65, 24.54) * mm});
            skLineSegment(sketch, "E22.3.1.6", {"start": v(-30.65, 24.54) * mm, "end": v(-27.11, 21) * mm});
            skLineSegment(sketch, "E22.3.1.7", {"start": v(-28.53, 29.49) * mm, "end": v(-32.06, 25.95) * mm});
            skLineSegment(sketch, "E22.3.1.8", {"start": v(-35.6, 29.49) * mm, "end": v(-32.06, 25.95) * mm});
            skLineSegment(sketch, "E22.3.2.0", {"start": v(-23.58, 14.54) * mm, "end": v(-27.11, 11) * mm});
            skLineSegment(sketch, "E22.3.2.1", {"start": v(-27.11, 18.07) * mm, "end": v(-23.58, 14.54) * mm});
            skLineSegment(sketch, "E22.3.2.2", {"start": v(-32.06, 23.02) * mm, "end": v(-35.6, 19.49) * mm});
            skLineSegment(sketch, "E22.3.2.3", {"start": v(-32.06, 23.02) * mm, "end": v(-28.53, 19.49) * mm});
            skLineSegment(sketch, "E22.3.2.4", {"start": v(-27.11, 18.07) * mm, "end": v(-30.65, 14.54) * mm});
            skLineSegment(sketch, "E22.3.2.5", {"start": v(-32.06, 15.95) * mm, "end": v(-30.65, 14.54) * mm});
            skLineSegment(sketch, "E22.3.2.6", {"start": v(-30.65, 14.54) * mm, "end": v(-27.11, 11) * mm});
            skLineSegment(sketch, "E22.3.2.7", {"start": v(-28.53, 19.49) * mm, "end": v(-32.06, 15.95) * mm});
            skLineSegment(sketch, "E22.3.2.8", {"start": v(-35.6, 19.49) * mm, "end": v(-32.06, 15.95) * mm});
            skLineSegment(sketch, "E22.3.3.0", {"start": v(-23.58, 4.54) * mm, "end": v(-27.11, 1) * mm});
            skLineSegment(sketch, "E22.3.3.1", {"start": v(-27.11, 8.07) * mm, "end": v(-23.58, 4.54) * mm});
            skLineSegment(sketch, "E22.3.3.2", {"start": v(-32.06, 13.02) * mm, "end": v(-35.6, 9.49) * mm});
            skLineSegment(sketch, "E22.3.3.3", {"start": v(-32.06, 13.02) * mm, "end": v(-28.53, 9.49) * mm});
            skLineSegment(sketch, "E22.3.3.4", {"start": v(-27.11, 8.07) * mm, "end": v(-30.65, 4.54) * mm});
            skLineSegment(sketch, "E22.3.3.5", {"start": v(-32.06, 5.95) * mm, "end": v(-30.65, 4.54) * mm});
            skLineSegment(sketch, "E22.3.3.6", {"start": v(-30.65, 4.54) * mm, "end": v(-27.11, 1) * mm});
            skLineSegment(sketch, "E22.3.3.7", {"start": v(-28.53, 9.49) * mm, "end": v(-32.06, 5.95) * mm});
            skLineSegment(sketch, "E22.3.3.8", {"start": v(-35.6, 9.49) * mm, "end": v(-32.06, 5.95) * mm});
            skLineSegment(sketch, "E22.4.0.0", {"start": v(-13.58, 34.54) * mm, "end": v(-17.11, 31) * mm});
            skLineSegment(sketch, "E22.4.0.1", {"start": v(-17.11, 38.07) * mm, "end": v(-13.58, 34.54) * mm});
            skLineSegment(sketch, "E22.4.0.2", {"start": v(-22.06, 43.02) * mm, "end": v(-25.6, 39.49) * mm});
            skLineSegment(sketch, "E22.4.0.3", {"start": v(-22.06, 43.02) * mm, "end": v(-18.53, 39.49) * mm});
            skLineSegment(sketch, "E22.4.0.4", {"start": v(-17.11, 38.07) * mm, "end": v(-20.65, 34.54) * mm});
            skLineSegment(sketch, "E22.4.0.5", {"start": v(-22.06, 35.95) * mm, "end": v(-20.65, 34.54) * mm});
            skLineSegment(sketch, "E22.4.0.6", {"start": v(-20.65, 34.54) * mm, "end": v(-17.11, 31) * mm});
            skLineSegment(sketch, "E22.4.0.7", {"start": v(-18.53, 39.49) * mm, "end": v(-22.06, 35.95) * mm});
            skLineSegment(sketch, "E22.4.0.8", {"start": v(-25.6, 39.49) * mm, "end": v(-22.06, 35.95) * mm});
            skLineSegment(sketch, "E22.4.1.0", {"start": v(-13.58, 24.54) * mm, "end": v(-17.11, 21) * mm});
            skLineSegment(sketch, "E22.4.1.1", {"start": v(-17.11, 28.07) * mm, "end": v(-13.58, 24.54) * mm});
            skLineSegment(sketch, "E22.4.1.2", {"start": v(-22.06, 33.02) * mm, "end": v(-25.6, 29.49) * mm});
            skLineSegment(sketch, "E22.4.1.3", {"start": v(-22.06, 33.02) * mm, "end": v(-18.53, 29.49) * mm});
            skLineSegment(sketch, "E22.4.1.4", {"start": v(-17.11, 28.07) * mm, "end": v(-20.65, 24.54) * mm});
            skLineSegment(sketch, "E22.4.1.5", {"start": v(-22.06, 25.95) * mm, "end": v(-20.65, 24.54) * mm});
            skLineSegment(sketch, "E22.4.1.6", {"start": v(-20.65, 24.54) * mm, "end": v(-17.11, 21) * mm});
            skLineSegment(sketch, "E22.4.1.7", {"start": v(-18.53, 29.49) * mm, "end": v(-22.06, 25.95) * mm});
            skLineSegment(sketch, "E22.4.1.8", {"start": v(-25.6, 29.49) * mm, "end": v(-22.06, 25.95) * mm});
            skLineSegment(sketch, "E22.4.2.0", {"start": v(-13.58, 14.54) * mm, "end": v(-17.11, 11) * mm});
            skLineSegment(sketch, "E22.4.2.1", {"start": v(-17.11, 18.07) * mm, "end": v(-13.58, 14.54) * mm});
            skLineSegment(sketch, "E22.4.2.2", {"start": v(-22.06, 23.02) * mm, "end": v(-25.6, 19.49) * mm});
            skLineSegment(sketch, "E22.4.2.3", {"start": v(-22.06, 23.02) * mm, "end": v(-18.53, 19.49) * mm});
            skLineSegment(sketch, "E22.4.2.4", {"start": v(-17.11, 18.07) * mm, "end": v(-20.65, 14.54) * mm});
            skLineSegment(sketch, "E22.4.2.5", {"start": v(-22.06, 15.95) * mm, "end": v(-20.65, 14.54) * mm});
            skLineSegment(sketch, "E22.4.2.6", {"start": v(-20.65, 14.54) * mm, "end": v(-17.11, 11) * mm});
            skLineSegment(sketch, "E22.4.2.7", {"start": v(-18.53, 19.49) * mm, "end": v(-22.06, 15.95) * mm});
            skLineSegment(sketch, "E22.4.2.8", {"start": v(-25.6, 19.49) * mm, "end": v(-22.06, 15.95) * mm});
            skLineSegment(sketch, "E22.4.3.0", {"start": v(-13.58, 4.54) * mm, "end": v(-17.11, 1) * mm});
            skLineSegment(sketch, "E22.4.3.1", {"start": v(-17.11, 8.07) * mm, "end": v(-13.58, 4.54) * mm});
            skLineSegment(sketch, "E22.4.3.2", {"start": v(-22.06, 13.02) * mm, "end": v(-25.6, 9.49) * mm});
            skLineSegment(sketch, "E22.4.3.3", {"start": v(-22.06, 13.02) * mm, "end": v(-18.53, 9.49) * mm});
            skLineSegment(sketch, "E22.4.3.4", {"start": v(-17.11, 8.07) * mm, "end": v(-20.65, 4.54) * mm});
            skLineSegment(sketch, "E22.4.3.5", {"start": v(-22.06, 5.95) * mm, "end": v(-20.65, 4.54) * mm});
            skLineSegment(sketch, "E22.4.3.6", {"start": v(-20.65, 4.54) * mm, "end": v(-17.11, 1) * mm});
            skLineSegment(sketch, "E22.4.3.7", {"start": v(-18.53, 9.49) * mm, "end": v(-22.06, 5.95) * mm});
            skLineSegment(sketch, "E22.4.3.8", {"start": v(-25.6, 9.49) * mm, "end": v(-22.06, 5.95) * mm});
            skLineSegment(sketch, "E22.5.0.0", {"start": v(-3.58, 34.54) * mm, "end": v(-7.11, 31) * mm});
            skLineSegment(sketch, "E22.5.0.1", {"start": v(-7.11, 38.07) * mm, "end": v(-3.58, 34.54) * mm});
            skLineSegment(sketch, "E22.5.0.2", {"start": v(-12.06, 43.02) * mm, "end": v(-15.6, 39.49) * mm});
            skLineSegment(sketch, "E22.5.0.3", {"start": v(-12.06, 43.02) * mm, "end": v(-8.53, 39.49) * mm});
            skLineSegment(sketch, "E22.5.0.4", {"start": v(-7.11, 38.07) * mm, "end": v(-10.65, 34.54) * mm});
            skLineSegment(sketch, "E22.5.0.5", {"start": v(-12.06, 35.95) * mm, "end": v(-10.65, 34.54) * mm});
            skLineSegment(sketch, "E22.5.0.6", {"start": v(-10.65, 34.54) * mm, "end": v(-7.11, 31) * mm});
            skLineSegment(sketch, "E22.5.0.7", {"start": v(-8.53, 39.49) * mm, "end": v(-12.06, 35.95) * mm});
            skLineSegment(sketch, "E22.5.0.8", {"start": v(-15.6, 39.49) * mm, "end": v(-12.06, 35.95) * mm});
            skLineSegment(sketch, "E22.5.1.0", {"start": v(-3.58, 24.54) * mm, "end": v(-7.11, 21) * mm});
            skLineSegment(sketch, "E22.5.1.1", {"start": v(-7.11, 28.07) * mm, "end": v(-3.58, 24.54) * mm});
            skLineSegment(sketch, "E22.5.1.2", {"start": v(-12.06, 33.02) * mm, "end": v(-15.6, 29.49) * mm});
            skLineSegment(sketch, "E22.5.1.3", {"start": v(-12.06, 33.02) * mm, "end": v(-8.53, 29.49) * mm});
            skLineSegment(sketch, "E22.5.1.4", {"start": v(-7.11, 28.07) * mm, "end": v(-10.65, 24.54) * mm});
            skLineSegment(sketch, "E22.5.1.5", {"start": v(-12.06, 25.95) * mm, "end": v(-10.65, 24.54) * mm});
            skLineSegment(sketch, "E22.5.1.6", {"start": v(-10.65, 24.54) * mm, "end": v(-7.11, 21) * mm});
            skLineSegment(sketch, "E22.5.1.7", {"start": v(-8.53, 29.49) * mm, "end": v(-12.06, 25.95) * mm});
            skLineSegment(sketch, "E22.5.1.8", {"start": v(-15.6, 29.49) * mm, "end": v(-12.06, 25.95) * mm});
            skLineSegment(sketch, "E22.5.2.0", {"start": v(-3.58, 14.54) * mm, "end": v(-7.11, 11) * mm});
            skLineSegment(sketch, "E22.5.2.1", {"start": v(-7.11, 18.07) * mm, "end": v(-3.58, 14.54) * mm});
            skLineSegment(sketch, "E22.5.2.2", {"start": v(-12.06, 23.02) * mm, "end": v(-15.6, 19.49) * mm});
            skLineSegment(sketch, "E22.5.2.3", {"start": v(-12.06, 23.02) * mm, "end": v(-8.53, 19.49) * mm});
            skLineSegment(sketch, "E22.5.2.4", {"start": v(-7.11, 18.07) * mm, "end": v(-10.65, 14.54) * mm});
            skLineSegment(sketch, "E22.5.2.5", {"start": v(-12.06, 15.95) * mm, "end": v(-10.65, 14.54) * mm});
            skLineSegment(sketch, "E22.5.2.6", {"start": v(-10.65, 14.54) * mm, "end": v(-7.11, 11) * mm});
            skLineSegment(sketch, "E22.5.2.7", {"start": v(-8.53, 19.49) * mm, "end": v(-12.06, 15.95) * mm});
            skLineSegment(sketch, "E22.5.2.8", {"start": v(-15.6, 19.49) * mm, "end": v(-12.06, 15.95) * mm});
            skLineSegment(sketch, "E22.5.3.0", {"start": v(-3.58, 4.54) * mm, "end": v(-7.11, 1) * mm});
            skLineSegment(sketch, "E22.5.3.1", {"start": v(-7.11, 8.07) * mm, "end": v(-3.58, 4.54) * mm});
            skLineSegment(sketch, "E22.5.3.2", {"start": v(-12.06, 13.02) * mm, "end": v(-15.6, 9.49) * mm});
            skLineSegment(sketch, "E22.5.3.3", {"start": v(-12.06, 13.02) * mm, "end": v(-8.53, 9.49) * mm});
            skLineSegment(sketch, "E22.5.3.4", {"start": v(-7.11, 8.07) * mm, "end": v(-10.65, 4.54) * mm});
            skLineSegment(sketch, "E22.5.3.5", {"start": v(-12.06, 5.95) * mm, "end": v(-10.65, 4.54) * mm});
            skLineSegment(sketch, "E22.5.3.6", {"start": v(-10.65, 4.54) * mm, "end": v(-7.11, 1) * mm});
            skLineSegment(sketch, "E22.5.3.7", {"start": v(-8.53, 9.49) * mm, "end": v(-12.06, 5.95) * mm});
            skLineSegment(sketch, "E22.5.3.8", {"start": v(-15.6, 9.49) * mm, "end": v(-12.06, 5.95) * mm});
            skLineSegment(sketch, "E22.6.0.0", {"start": v(6.42, 34.54) * mm, "end": v(2.89, 31) * mm});
            skLineSegment(sketch, "E22.6.0.1", {"start": v(2.89, 38.07) * mm, "end": v(6.42, 34.54) * mm});
            skLineSegment(sketch, "E22.6.0.2", {"start": v(-2.06, 43.02) * mm, "end": v(-5.6, 39.49) * mm});
            skLineSegment(sketch, "E22.6.0.3", {"start": v(-2.06, 43.02) * mm, "end": v(1.47, 39.49) * mm});
            skLineSegment(sketch, "E22.6.0.4", {"start": v(2.89, 38.07) * mm, "end": v(-0.65, 34.54) * mm});
            skLineSegment(sketch, "E22.6.0.5", {"start": v(-2.06, 35.95) * mm, "end": v(-0.65, 34.54) * mm});
            skLineSegment(sketch, "E22.6.0.6", {"start": v(-0.65, 34.54) * mm, "end": v(2.89, 31) * mm});
            skLineSegment(sketch, "E22.6.0.7", {"start": v(1.47, 39.49) * mm, "end": v(-2.06, 35.95) * mm});
            skLineSegment(sketch, "E22.6.0.8", {"start": v(-5.6, 39.49) * mm, "end": v(-2.06, 35.95) * mm});
            skLineSegment(sketch, "E22.6.1.0", {"start": v(6.42, 24.54) * mm, "end": v(2.89, 21) * mm});
            skLineSegment(sketch, "E22.6.1.1", {"start": v(2.89, 28.07) * mm, "end": v(6.42, 24.54) * mm});
            skLineSegment(sketch, "E22.6.1.2", {"start": v(-2.06, 33.02) * mm, "end": v(-5.6, 29.49) * mm});
            skLineSegment(sketch, "E22.6.1.3", {"start": v(-2.06, 33.02) * mm, "end": v(1.47, 29.49) * mm});
            skLineSegment(sketch, "E22.6.1.4", {"start": v(2.89, 28.07) * mm, "end": v(-0.65, 24.54) * mm});
            skLineSegment(sketch, "E22.6.1.5", {"start": v(-2.06, 25.95) * mm, "end": v(-0.65, 24.54) * mm});
            skLineSegment(sketch, "E22.6.1.6", {"start": v(-0.65, 24.54) * mm, "end": v(2.89, 21) * mm});
            skLineSegment(sketch, "E22.6.1.7", {"start": v(1.47, 29.49) * mm, "end": v(-2.06, 25.95) * mm});
            skLineSegment(sketch, "E22.6.1.8", {"start": v(-5.6, 29.49) * mm, "end": v(-2.06, 25.95) * mm});
            skLineSegment(sketch, "E22.6.2.0", {"start": v(6.42, 14.54) * mm, "end": v(2.89, 11) * mm});
            skLineSegment(sketch, "E22.6.2.1", {"start": v(2.89, 18.07) * mm, "end": v(6.42, 14.54) * mm});
            skLineSegment(sketch, "E22.6.2.2", {"start": v(-2.06, 23.02) * mm, "end": v(-5.6, 19.49) * mm});
            skLineSegment(sketch, "E22.6.2.3", {"start": v(-2.06, 23.02) * mm, "end": v(1.47, 19.49) * mm});
            skLineSegment(sketch, "E22.6.2.4", {"start": v(2.89, 18.07) * mm, "end": v(-0.65, 14.54) * mm});
            skLineSegment(sketch, "E22.6.2.5", {"start": v(-2.06, 15.95) * mm, "end": v(-0.65, 14.54) * mm});
            skLineSegment(sketch, "E22.6.2.6", {"start": v(-0.65, 14.54) * mm, "end": v(2.89, 11) * mm});
            skLineSegment(sketch, "E22.6.2.7", {"start": v(1.47, 19.49) * mm, "end": v(-2.06, 15.95) * mm});
            skLineSegment(sketch, "E22.6.2.8", {"start": v(-5.6, 19.49) * mm, "end": v(-2.06, 15.95) * mm});
            skLineSegment(sketch, "E22.6.3.0", {"start": v(6.42, 4.54) * mm, "end": v(2.89, 1) * mm});
            skLineSegment(sketch, "E22.6.3.1", {"start": v(2.89, 8.07) * mm, "end": v(6.42, 4.54) * mm});
            skLineSegment(sketch, "E22.6.3.2", {"start": v(-2.06, 13.02) * mm, "end": v(-5.6, 9.49) * mm});
            skLineSegment(sketch, "E22.6.3.3", {"start": v(-2.06, 13.02) * mm, "end": v(1.47, 9.49) * mm});
            skLineSegment(sketch, "E22.6.3.4", {"start": v(2.89, 8.07) * mm, "end": v(-0.65, 4.54) * mm});
            skLineSegment(sketch, "E22.6.3.5", {"start": v(-2.06, 5.95) * mm, "end": v(-0.65, 4.54) * mm});
            skLineSegment(sketch, "E22.6.3.6", {"start": v(-0.65, 4.54) * mm, "end": v(2.89, 1) * mm});
            skLineSegment(sketch, "E22.6.3.7", {"start": v(1.47, 9.49) * mm, "end": v(-2.06, 5.95) * mm});
            skLineSegment(sketch, "E22.6.3.8", {"start": v(-5.6, 9.49) * mm, "end": v(-2.06, 5.95) * mm});
            skLineSegment(sketch, "E22.7.0.0", {"start": v(16.42, 34.54) * mm, "end": v(12.89, 31) * mm});
            skLineSegment(sketch, "E22.7.0.1", {"start": v(12.89, 38.07) * mm, "end": v(16.42, 34.54) * mm});
            skLineSegment(sketch, "E22.7.0.2", {"start": v(7.94, 43.02) * mm, "end": v(4.4, 39.49) * mm});
            skLineSegment(sketch, "E22.7.0.3", {"start": v(7.94, 43.02) * mm, "end": v(11.47, 39.49) * mm});
            skLineSegment(sketch, "E22.7.0.4", {"start": v(12.89, 38.07) * mm, "end": v(9.35, 34.54) * mm});
            skLineSegment(sketch, "E22.7.0.5", {"start": v(7.94, 35.95) * mm, "end": v(9.35, 34.54) * mm});
            skLineSegment(sketch, "E22.7.0.6", {"start": v(9.35, 34.54) * mm, "end": v(12.89, 31) * mm});
            skLineSegment(sketch, "E22.7.0.7", {"start": v(11.47, 39.49) * mm, "end": v(7.94, 35.95) * mm});
            skLineSegment(sketch, "E22.7.0.8", {"start": v(4.4, 39.49) * mm, "end": v(7.94, 35.95) * mm});
            skLineSegment(sketch, "E22.7.1.0", {"start": v(16.42, 24.54) * mm, "end": v(12.89, 21) * mm});
            skLineSegment(sketch, "E22.7.1.1", {"start": v(12.89, 28.07) * mm, "end": v(16.42, 24.54) * mm});
            skLineSegment(sketch, "E22.7.1.2", {"start": v(7.94, 33.02) * mm, "end": v(4.4, 29.49) * mm});
            skLineSegment(sketch, "E22.7.1.3", {"start": v(7.94, 33.02) * mm, "end": v(11.47, 29.49) * mm});
            skLineSegment(sketch, "E22.7.1.4", {"start": v(12.89, 28.07) * mm, "end": v(9.35, 24.54) * mm});
            skLineSegment(sketch, "E22.7.1.5", {"start": v(7.94, 25.95) * mm, "end": v(9.35, 24.54) * mm});
            skLineSegment(sketch, "E22.7.1.6", {"start": v(9.35, 24.54) * mm, "end": v(12.89, 21) * mm});
            skLineSegment(sketch, "E22.7.1.7", {"start": v(11.47, 29.49) * mm, "end": v(7.94, 25.95) * mm});
            skLineSegment(sketch, "E22.7.1.8", {"start": v(4.4, 29.49) * mm, "end": v(7.94, 25.95) * mm});
            skLineSegment(sketch, "E22.7.2.0", {"start": v(16.42, 14.54) * mm, "end": v(12.89, 11) * mm});
            skLineSegment(sketch, "E22.7.2.1", {"start": v(12.89, 18.07) * mm, "end": v(16.42, 14.54) * mm});
            skLineSegment(sketch, "E22.7.2.2", {"start": v(7.94, 23.02) * mm, "end": v(4.4, 19.49) * mm});
            skLineSegment(sketch, "E22.7.2.3", {"start": v(7.94, 23.02) * mm, "end": v(11.47, 19.49) * mm});
            skLineSegment(sketch, "E22.7.2.4", {"start": v(12.89, 18.07) * mm, "end": v(9.35, 14.54) * mm});
            skLineSegment(sketch, "E22.7.2.5", {"start": v(7.94, 15.95) * mm, "end": v(9.35, 14.54) * mm});
            skLineSegment(sketch, "E22.7.2.6", {"start": v(9.35, 14.54) * mm, "end": v(12.89, 11) * mm});
            skLineSegment(sketch, "E22.7.2.7", {"start": v(11.47, 19.49) * mm, "end": v(7.94, 15.95) * mm});
            skLineSegment(sketch, "E22.7.2.8", {"start": v(4.4, 19.49) * mm, "end": v(7.94, 15.95) * mm});
            skLineSegment(sketch, "E22.7.3.0", {"start": v(16.42, 4.54) * mm, "end": v(12.89, 1) * mm});
            skLineSegment(sketch, "E22.7.3.1", {"start": v(12.89, 8.07) * mm, "end": v(16.42, 4.54) * mm});
            skLineSegment(sketch, "E22.7.3.2", {"start": v(7.94, 13.02) * mm, "end": v(4.4, 9.49) * mm});
            skLineSegment(sketch, "E22.7.3.3", {"start": v(7.94, 13.02) * mm, "end": v(11.47, 9.49) * mm});
            skLineSegment(sketch, "E22.7.3.4", {"start": v(12.89, 8.07) * mm, "end": v(9.35, 4.54) * mm});
            skLineSegment(sketch, "E22.7.3.5", {"start": v(7.94, 5.95) * mm, "end": v(9.35, 4.54) * mm});
            skLineSegment(sketch, "E22.7.3.6", {"start": v(9.35, 4.54) * mm, "end": v(12.89, 1) * mm});
            skLineSegment(sketch, "E22.7.3.7", {"start": v(11.47, 9.49) * mm, "end": v(7.94, 5.95) * mm});
            skLineSegment(sketch, "E22.7.3.8", {"start": v(4.4, 9.49) * mm, "end": v(7.94, 5.95) * mm});
            skLineSegment(sketch, "E22.8.0.0", {"start": v(26.42, 34.54) * mm, "end": v(22.89, 31) * mm});
            skLineSegment(sketch, "E22.8.0.1", {"start": v(22.89, 38.07) * mm, "end": v(26.42, 34.54) * mm});
            skLineSegment(sketch, "E22.8.0.2", {"start": v(17.94, 43.02) * mm, "end": v(14.4, 39.49) * mm});
            skLineSegment(sketch, "E22.8.0.3", {"start": v(17.94, 43.02) * mm, "end": v(21.47, 39.49) * mm});
            skLineSegment(sketch, "E22.8.0.4", {"start": v(22.89, 38.07) * mm, "end": v(19.35, 34.54) * mm});
            skLineSegment(sketch, "E22.8.0.5", {"start": v(17.94, 35.95) * mm, "end": v(19.35, 34.54) * mm});
            skLineSegment(sketch, "E22.8.0.6", {"start": v(19.35, 34.54) * mm, "end": v(22.89, 31) * mm});
            skLineSegment(sketch, "E22.8.0.7", {"start": v(21.47, 39.49) * mm, "end": v(17.94, 35.95) * mm});
            skLineSegment(sketch, "E22.8.0.8", {"start": v(14.4, 39.49) * mm, "end": v(17.94, 35.95) * mm});
            skLineSegment(sketch, "E22.8.1.0", {"start": v(26.42, 24.54) * mm, "end": v(22.89, 21) * mm});
            skLineSegment(sketch, "E22.8.1.1", {"start": v(22.89, 28.07) * mm, "end": v(26.42, 24.54) * mm});
            skLineSegment(sketch, "E22.8.1.2", {"start": v(17.94, 33.02) * mm, "end": v(14.4, 29.49) * mm});
            skLineSegment(sketch, "E22.8.1.3", {"start": v(17.94, 33.02) * mm, "end": v(21.47, 29.49) * mm});
            skLineSegment(sketch, "E22.8.1.4", {"start": v(22.89, 28.07) * mm, "end": v(19.35, 24.54) * mm});
            skLineSegment(sketch, "E22.8.1.5", {"start": v(17.94, 25.95) * mm, "end": v(19.35, 24.54) * mm});
            skLineSegment(sketch, "E22.8.1.6", {"start": v(19.35, 24.54) * mm, "end": v(22.89, 21) * mm});
            skLineSegment(sketch, "E22.8.1.7", {"start": v(21.47, 29.49) * mm, "end": v(17.94, 25.95) * mm});
            skLineSegment(sketch, "E22.8.1.8", {"start": v(14.4, 29.49) * mm, "end": v(17.94, 25.95) * mm});
            skLineSegment(sketch, "E22.8.2.0", {"start": v(26.42, 14.54) * mm, "end": v(22.89, 11) * mm});
            skLineSegment(sketch, "E22.8.2.1", {"start": v(22.89, 18.07) * mm, "end": v(26.42, 14.54) * mm});
            skLineSegment(sketch, "E22.8.2.2", {"start": v(17.94, 23.02) * mm, "end": v(14.4, 19.49) * mm});
            skLineSegment(sketch, "E22.8.2.3", {"start": v(17.94, 23.02) * mm, "end": v(21.47, 19.49) * mm});
            skLineSegment(sketch, "E22.8.2.4", {"start": v(22.89, 18.07) * mm, "end": v(19.35, 14.54) * mm});
            skLineSegment(sketch, "E22.8.2.5", {"start": v(17.94, 15.95) * mm, "end": v(19.35, 14.54) * mm});
            skLineSegment(sketch, "E22.8.2.6", {"start": v(19.35, 14.54) * mm, "end": v(22.89, 11) * mm});
            skLineSegment(sketch, "E22.8.2.7", {"start": v(21.47, 19.49) * mm, "end": v(17.94, 15.95) * mm});
            skLineSegment(sketch, "E22.8.2.8", {"start": v(14.4, 19.49) * mm, "end": v(17.94, 15.95) * mm});
            skLineSegment(sketch, "E22.8.3.0", {"start": v(26.42, 4.54) * mm, "end": v(22.89, 1) * mm});
            skLineSegment(sketch, "E22.8.3.1", {"start": v(22.89, 8.07) * mm, "end": v(26.42, 4.54) * mm});
            skLineSegment(sketch, "E22.8.3.2", {"start": v(17.94, 13.02) * mm, "end": v(14.4, 9.49) * mm});
            skLineSegment(sketch, "E22.8.3.3", {"start": v(17.94, 13.02) * mm, "end": v(21.47, 9.49) * mm});
            skLineSegment(sketch, "E22.8.3.4", {"start": v(22.89, 8.07) * mm, "end": v(19.35, 4.54) * mm});
            skLineSegment(sketch, "E22.8.3.5", {"start": v(17.94, 5.95) * mm, "end": v(19.35, 4.54) * mm});
            skLineSegment(sketch, "E22.8.3.6", {"start": v(19.35, 4.54) * mm, "end": v(22.89, 1) * mm});
            skLineSegment(sketch, "E22.8.3.7", {"start": v(21.47, 9.49) * mm, "end": v(17.94, 5.95) * mm});
            skLineSegment(sketch, "E22.8.3.8", {"start": v(14.4, 9.49) * mm, "end": v(17.94, 5.95) * mm});
            skLineSegment(sketch, "E22.9.0.0", {"start": v(36.42, 34.54) * mm, "end": v(32.89, 31) * mm});
            skLineSegment(sketch, "E22.9.0.1", {"start": v(32.89, 38.07) * mm, "end": v(36.42, 34.54) * mm});
            skLineSegment(sketch, "E22.9.0.2", {"start": v(27.94, 43.02) * mm, "end": v(24.4, 39.49) * mm});
            skLineSegment(sketch, "E22.9.0.3", {"start": v(27.94, 43.02) * mm, "end": v(31.47, 39.49) * mm});
            skLineSegment(sketch, "E22.9.0.4", {"start": v(32.89, 38.07) * mm, "end": v(29.35, 34.54) * mm});
            skLineSegment(sketch, "E22.9.0.5", {"start": v(27.94, 35.95) * mm, "end": v(29.35, 34.54) * mm});
            skLineSegment(sketch, "E22.9.0.6", {"start": v(29.35, 34.54) * mm, "end": v(32.89, 31) * mm});
            skLineSegment(sketch, "E22.9.0.7", {"start": v(31.47, 39.49) * mm, "end": v(27.94, 35.95) * mm});
            skLineSegment(sketch, "E22.9.0.8", {"start": v(24.4, 39.49) * mm, "end": v(27.94, 35.95) * mm});
            skLineSegment(sketch, "E22.9.1.0", {"start": v(36.42, 24.54) * mm, "end": v(32.89, 21) * mm});
            skLineSegment(sketch, "E22.9.1.1", {"start": v(32.89, 28.07) * mm, "end": v(36.42, 24.54) * mm});
            skLineSegment(sketch, "E22.9.1.2", {"start": v(27.94, 33.02) * mm, "end": v(24.4, 29.49) * mm});
            skLineSegment(sketch, "E22.9.1.3", {"start": v(27.94, 33.02) * mm, "end": v(31.47, 29.49) * mm});
            skLineSegment(sketch, "E22.9.1.4", {"start": v(32.89, 28.07) * mm, "end": v(29.35, 24.54) * mm});
            skLineSegment(sketch, "E22.9.1.5", {"start": v(27.94, 25.95) * mm, "end": v(29.35, 24.54) * mm});
            skLineSegment(sketch, "E22.9.1.6", {"start": v(29.35, 24.54) * mm, "end": v(32.89, 21) * mm});
            skLineSegment(sketch, "E22.9.1.7", {"start": v(31.47, 29.49) * mm, "end": v(27.94, 25.95) * mm});
            skLineSegment(sketch, "E22.9.1.8", {"start": v(24.4, 29.49) * mm, "end": v(27.94, 25.95) * mm});
            skLineSegment(sketch, "E22.9.2.0", {"start": v(36.42, 14.54) * mm, "end": v(32.89, 11) * mm});
            skLineSegment(sketch, "E22.9.2.1", {"start": v(32.89, 18.07) * mm, "end": v(36.42, 14.54) * mm});
            skLineSegment(sketch, "E22.9.2.2", {"start": v(27.94, 23.02) * mm, "end": v(24.4, 19.49) * mm});
            skLineSegment(sketch, "E22.9.2.3", {"start": v(27.94, 23.02) * mm, "end": v(31.47, 19.49) * mm});
            skLineSegment(sketch, "E22.9.2.4", {"start": v(32.89, 18.07) * mm, "end": v(29.35, 14.54) * mm});
            skLineSegment(sketch, "E22.9.2.5", {"start": v(27.94, 15.95) * mm, "end": v(29.35, 14.54) * mm});
            skLineSegment(sketch, "E22.9.2.6", {"start": v(29.35, 14.54) * mm, "end": v(32.89, 11) * mm});
            skLineSegment(sketch, "E22.9.2.7", {"start": v(31.47, 19.49) * mm, "end": v(27.94, 15.95) * mm});
            skLineSegment(sketch, "E22.9.2.8", {"start": v(24.4, 19.49) * mm, "end": v(27.94, 15.95) * mm});
            skLineSegment(sketch, "E22.9.3.0", {"start": v(36.42, 4.54) * mm, "end": v(32.89, 1) * mm});
            skLineSegment(sketch, "E22.9.3.1", {"start": v(32.89, 8.07) * mm, "end": v(36.42, 4.54) * mm});
            skLineSegment(sketch, "E22.9.3.2", {"start": v(27.94, 13.02) * mm, "end": v(24.4, 9.49) * mm});
            skLineSegment(sketch, "E22.9.3.3", {"start": v(27.94, 13.02) * mm, "end": v(31.47, 9.49) * mm});
            skLineSegment(sketch, "E22.9.3.4", {"start": v(32.89, 8.07) * mm, "end": v(29.35, 4.54) * mm});
            skLineSegment(sketch, "E22.9.3.5", {"start": v(27.94, 5.95) * mm, "end": v(29.35, 4.54) * mm});
            skLineSegment(sketch, "E22.9.3.6", {"start": v(29.35, 4.54) * mm, "end": v(32.89, 1) * mm});
            skLineSegment(sketch, "E22.9.3.7", {"start": v(31.47, 9.49) * mm, "end": v(27.94, 5.95) * mm});
            skLineSegment(sketch, "E22.9.3.8", {"start": v(24.4, 9.49) * mm, "end": v(27.94, 5.95) * mm});
            skLineSegment(sketch, "E22.10.0.0", {"start": v(46.42, 34.54) * mm, "end": v(42.89, 31) * mm});
            skLineSegment(sketch, "E22.10.0.1", {"start": v(42.89, 38.07) * mm, "end": v(46.42, 34.54) * mm});
            skLineSegment(sketch, "E22.10.0.2", {"start": v(37.94, 43.02) * mm, "end": v(34.4, 39.49) * mm});
            skLineSegment(sketch, "E22.10.0.3", {"start": v(37.94, 43.02) * mm, "end": v(41.47, 39.49) * mm});
            skLineSegment(sketch, "E22.10.0.4", {"start": v(42.89, 38.07) * mm, "end": v(39.35, 34.54) * mm});
            skLineSegment(sketch, "E22.10.0.5", {"start": v(37.94, 35.95) * mm, "end": v(39.35, 34.54) * mm});
            skLineSegment(sketch, "E22.10.0.6", {"start": v(39.35, 34.54) * mm, "end": v(42.89, 31) * mm});
            skLineSegment(sketch, "E22.10.0.7", {"start": v(41.47, 39.49) * mm, "end": v(37.94, 35.95) * mm});
            skLineSegment(sketch, "E22.10.0.8", {"start": v(34.4, 39.49) * mm, "end": v(37.94, 35.95) * mm});
            skLineSegment(sketch, "E22.10.1.0", {"start": v(46.42, 24.54) * mm, "end": v(42.89, 21) * mm});
            skLineSegment(sketch, "E22.10.1.1", {"start": v(42.89, 28.07) * mm, "end": v(46.42, 24.54) * mm});
            skLineSegment(sketch, "E22.10.1.2", {"start": v(37.94, 33.02) * mm, "end": v(34.4, 29.49) * mm});
            skLineSegment(sketch, "E22.10.1.3", {"start": v(37.94, 33.02) * mm, "end": v(41.47, 29.49) * mm});
            skLineSegment(sketch, "E22.10.1.4", {"start": v(42.89, 28.07) * mm, "end": v(39.35, 24.54) * mm});
            skLineSegment(sketch, "E22.10.1.5", {"start": v(37.94, 25.95) * mm, "end": v(39.35, 24.54) * mm});
            skLineSegment(sketch, "E22.10.1.6", {"start": v(39.35, 24.54) * mm, "end": v(42.89, 21) * mm});
            skLineSegment(sketch, "E22.10.1.7", {"start": v(41.47, 29.49) * mm, "end": v(37.94, 25.95) * mm});
            skLineSegment(sketch, "E22.10.1.8", {"start": v(34.4, 29.49) * mm, "end": v(37.94, 25.95) * mm});
            skLineSegment(sketch, "E22.10.2.0", {"start": v(46.42, 14.54) * mm, "end": v(42.89, 11) * mm});
            skLineSegment(sketch, "E22.10.2.1", {"start": v(42.89, 18.07) * mm, "end": v(46.42, 14.54) * mm});
            skLineSegment(sketch, "E22.10.2.2", {"start": v(37.94, 23.02) * mm, "end": v(34.4, 19.49) * mm});
            skLineSegment(sketch, "E22.10.2.3", {"start": v(37.94, 23.02) * mm, "end": v(41.47, 19.49) * mm});
            skLineSegment(sketch, "E22.10.2.4", {"start": v(42.89, 18.07) * mm, "end": v(39.35, 14.54) * mm});
            skLineSegment(sketch, "E22.10.2.5", {"start": v(37.94, 15.95) * mm, "end": v(39.35, 14.54) * mm});
            skLineSegment(sketch, "E22.10.2.6", {"start": v(39.35, 14.54) * mm, "end": v(42.89, 11) * mm});
            skLineSegment(sketch, "E22.10.2.7", {"start": v(41.47, 19.49) * mm, "end": v(37.94, 15.95) * mm});
            skLineSegment(sketch, "E22.10.2.8", {"start": v(34.4, 19.49) * mm, "end": v(37.94, 15.95) * mm});
            skLineSegment(sketch, "E22.10.3.0", {"start": v(46.42, 4.54) * mm, "end": v(42.89, 1) * mm});
            skLineSegment(sketch, "E22.10.3.1", {"start": v(42.89, 8.07) * mm, "end": v(46.42, 4.54) * mm});
            skLineSegment(sketch, "E22.10.3.2", {"start": v(37.94, 13.02) * mm, "end": v(34.4, 9.49) * mm});
            skLineSegment(sketch, "E22.10.3.3", {"start": v(37.94, 13.02) * mm, "end": v(41.47, 9.49) * mm});
            skLineSegment(sketch, "E22.10.3.4", {"start": v(42.89, 8.07) * mm, "end": v(39.35, 4.54) * mm});
            skLineSegment(sketch, "E22.10.3.5", {"start": v(37.94, 5.95) * mm, "end": v(39.35, 4.54) * mm});
            skLineSegment(sketch, "E22.10.3.6", {"start": v(39.35, 4.54) * mm, "end": v(42.89, 1) * mm});
            skLineSegment(sketch, "E22.10.3.7", {"start": v(41.47, 9.49) * mm, "end": v(37.94, 5.95) * mm});
            skLineSegment(sketch, "E22.10.3.8", {"start": v(34.4, 9.49) * mm, "end": v(37.94, 5.95) * mm});
            skLineSegment(sketch, "E22.11.0.0", {"start": v(56.42, 34.54) * mm, "end": v(52.89, 31) * mm});
            skLineSegment(sketch, "E22.11.0.1", {"start": v(52.89, 38.07) * mm, "end": v(56.42, 34.54) * mm});
            skLineSegment(sketch, "E22.11.0.2", {"start": v(47.94, 43.02) * mm, "end": v(44.4, 39.49) * mm});
            skLineSegment(sketch, "E22.11.0.3", {"start": v(47.94, 43.02) * mm, "end": v(51.47, 39.49) * mm});
            skLineSegment(sketch, "E22.11.0.4", {"start": v(52.89, 38.07) * mm, "end": v(49.35, 34.54) * mm});
            skLineSegment(sketch, "E22.11.0.5", {"start": v(47.94, 35.95) * mm, "end": v(49.35, 34.54) * mm});
            skLineSegment(sketch, "E22.11.0.6", {"start": v(49.35, 34.54) * mm, "end": v(52.89, 31) * mm});
            skLineSegment(sketch, "E22.11.0.7", {"start": v(51.47, 39.49) * mm, "end": v(47.94, 35.95) * mm});
            skLineSegment(sketch, "E22.11.0.8", {"start": v(44.4, 39.49) * mm, "end": v(47.94, 35.95) * mm});
            skLineSegment(sketch, "E22.11.1.0", {"start": v(56.42, 24.54) * mm, "end": v(52.89, 21) * mm});
            skLineSegment(sketch, "E22.11.1.1", {"start": v(52.89, 28.07) * mm, "end": v(56.42, 24.54) * mm});
            skLineSegment(sketch, "E22.11.1.2", {"start": v(47.94, 33.02) * mm, "end": v(44.4, 29.49) * mm});
            skLineSegment(sketch, "E22.11.1.3", {"start": v(47.94, 33.02) * mm, "end": v(51.47, 29.49) * mm});
            skLineSegment(sketch, "E22.11.1.4", {"start": v(52.89, 28.07) * mm, "end": v(49.35, 24.54) * mm});
            skLineSegment(sketch, "E22.11.1.5", {"start": v(47.94, 25.95) * mm, "end": v(49.35, 24.54) * mm});
            skLineSegment(sketch, "E22.11.1.6", {"start": v(49.35, 24.54) * mm, "end": v(52.89, 21) * mm});
            skLineSegment(sketch, "E22.11.1.7", {"start": v(51.47, 29.49) * mm, "end": v(47.94, 25.95) * mm});
            skLineSegment(sketch, "E22.11.1.8", {"start": v(44.4, 29.49) * mm, "end": v(47.94, 25.95) * mm});
            skLineSegment(sketch, "E22.11.2.0", {"start": v(56.42, 14.54) * mm, "end": v(52.89, 11) * mm});
            skLineSegment(sketch, "E22.11.2.1", {"start": v(52.89, 18.07) * mm, "end": v(56.42, 14.54) * mm});
            skLineSegment(sketch, "E22.11.2.2", {"start": v(47.94, 23.02) * mm, "end": v(44.4, 19.49) * mm});
            skLineSegment(sketch, "E22.11.2.3", {"start": v(47.94, 23.02) * mm, "end": v(51.47, 19.49) * mm});
            skLineSegment(sketch, "E22.11.2.4", {"start": v(52.89, 18.07) * mm, "end": v(49.35, 14.54) * mm});
            skLineSegment(sketch, "E22.11.2.5", {"start": v(47.94, 15.95) * mm, "end": v(49.35, 14.54) * mm});
            skLineSegment(sketch, "E22.11.2.6", {"start": v(49.35, 14.54) * mm, "end": v(52.89, 11) * mm});
            skLineSegment(sketch, "E22.11.2.7", {"start": v(51.47, 19.49) * mm, "end": v(47.94, 15.95) * mm});
            skLineSegment(sketch, "E22.11.2.8", {"start": v(44.4, 19.49) * mm, "end": v(47.94, 15.95) * mm});
            skLineSegment(sketch, "E22.11.3.0", {"start": v(56.42, 4.54) * mm, "end": v(52.89, 1) * mm});
            skLineSegment(sketch, "E22.11.3.1", {"start": v(52.89, 8.07) * mm, "end": v(56.42, 4.54) * mm});
            skLineSegment(sketch, "E22.11.3.2", {"start": v(47.94, 13.02) * mm, "end": v(44.4, 9.49) * mm});
            skLineSegment(sketch, "E22.11.3.3", {"start": v(47.94, 13.02) * mm, "end": v(51.47, 9.49) * mm});
            skLineSegment(sketch, "E22.11.3.4", {"start": v(52.89, 8.07) * mm, "end": v(49.35, 4.54) * mm});
            skLineSegment(sketch, "E22.11.3.5", {"start": v(47.94, 5.95) * mm, "end": v(49.35, 4.54) * mm});
            skLineSegment(sketch, "E22.11.3.6", {"start": v(49.35, 4.54) * mm, "end": v(52.89, 1) * mm});
            skLineSegment(sketch, "E22.11.3.7", {"start": v(51.47, 9.49) * mm, "end": v(47.94, 5.95) * mm});
            skLineSegment(sketch, "E22.11.3.8", {"start": v(44.4, 9.49) * mm, "end": v(47.94, 5.95) * mm});
            skLineSegment(sketch, "E22.12.0.0", {"start": v(66.42, 34.54) * mm, "end": v(62.89, 31) * mm});
            skLineSegment(sketch, "E22.12.0.1", {"start": v(62.89, 38.07) * mm, "end": v(66.42, 34.54) * mm});
            skLineSegment(sketch, "E22.12.0.2", {"start": v(57.94, 43.02) * mm, "end": v(54.4, 39.49) * mm});
            skLineSegment(sketch, "E22.12.0.3", {"start": v(57.94, 43.02) * mm, "end": v(61.47, 39.49) * mm});
            skLineSegment(sketch, "E22.12.0.4", {"start": v(62.89, 38.07) * mm, "end": v(59.35, 34.54) * mm});
            skLineSegment(sketch, "E22.12.0.5", {"start": v(57.94, 35.95) * mm, "end": v(59.35, 34.54) * mm});
            skLineSegment(sketch, "E22.12.0.6", {"start": v(59.35, 34.54) * mm, "end": v(62.89, 31) * mm});
            skLineSegment(sketch, "E22.12.0.7", {"start": v(61.47, 39.49) * mm, "end": v(57.94, 35.95) * mm});
            skLineSegment(sketch, "E22.12.0.8", {"start": v(54.4, 39.49) * mm, "end": v(57.94, 35.95) * mm});
            skLineSegment(sketch, "E22.12.1.0", {"start": v(66.42, 24.54) * mm, "end": v(62.89, 21) * mm});
            skLineSegment(sketch, "E22.12.1.1", {"start": v(62.89, 28.07) * mm, "end": v(66.42, 24.54) * mm});
            skLineSegment(sketch, "E22.12.1.2", {"start": v(57.94, 33.02) * mm, "end": v(54.4, 29.49) * mm});
            skLineSegment(sketch, "E22.12.1.3", {"start": v(57.94, 33.02) * mm, "end": v(61.47, 29.49) * mm});
            skLineSegment(sketch, "E22.12.1.4", {"start": v(62.89, 28.07) * mm, "end": v(59.35, 24.54) * mm});
            skLineSegment(sketch, "E22.12.1.5", {"start": v(57.94, 25.95) * mm, "end": v(59.35, 24.54) * mm});
            skLineSegment(sketch, "E22.12.1.6", {"start": v(59.35, 24.54) * mm, "end": v(62.89, 21) * mm});
            skLineSegment(sketch, "E22.12.1.7", {"start": v(61.47, 29.49) * mm, "end": v(57.94, 25.95) * mm});
            skLineSegment(sketch, "E22.12.1.8", {"start": v(54.4, 29.49) * mm, "end": v(57.94, 25.95) * mm});
            skLineSegment(sketch, "E22.12.2.0", {"start": v(66.42, 14.54) * mm, "end": v(62.89, 11) * mm});
            skLineSegment(sketch, "E22.12.2.1", {"start": v(62.89, 18.07) * mm, "end": v(66.42, 14.54) * mm});
            skLineSegment(sketch, "E22.12.2.2", {"start": v(57.94, 23.02) * mm, "end": v(54.4, 19.49) * mm});
            skLineSegment(sketch, "E22.12.2.3", {"start": v(57.94, 23.02) * mm, "end": v(61.47, 19.49) * mm});
            skLineSegment(sketch, "E22.12.2.4", {"start": v(62.89, 18.07) * mm, "end": v(59.35, 14.54) * mm});
            skLineSegment(sketch, "E22.12.2.5", {"start": v(57.94, 15.95) * mm, "end": v(59.35, 14.54) * mm});
            skLineSegment(sketch, "E22.12.2.6", {"start": v(59.35, 14.54) * mm, "end": v(62.89, 11) * mm});
            skLineSegment(sketch, "E22.12.2.7", {"start": v(61.47, 19.49) * mm, "end": v(57.94, 15.95) * mm});
            skLineSegment(sketch, "E22.12.2.8", {"start": v(54.4, 19.49) * mm, "end": v(57.94, 15.95) * mm});
            skLineSegment(sketch, "E22.12.3.0", {"start": v(66.42, 4.54) * mm, "end": v(62.89, 1) * mm});
            skLineSegment(sketch, "E22.12.3.1", {"start": v(62.89, 8.07) * mm, "end": v(66.42, 4.54) * mm});
            skLineSegment(sketch, "E22.12.3.2", {"start": v(57.94, 13.02) * mm, "end": v(54.4, 9.49) * mm});
            skLineSegment(sketch, "E22.12.3.3", {"start": v(57.94, 13.02) * mm, "end": v(61.47, 9.49) * mm});
            skLineSegment(sketch, "E22.12.3.4", {"start": v(62.89, 8.07) * mm, "end": v(59.35, 4.54) * mm});
            skLineSegment(sketch, "E22.12.3.5", {"start": v(57.94, 5.95) * mm, "end": v(59.35, 4.54) * mm});
            skLineSegment(sketch, "E22.12.3.6", {"start": v(59.35, 4.54) * mm, "end": v(62.89, 1) * mm});
            skLineSegment(sketch, "E22.12.3.7", {"start": v(61.47, 9.49) * mm, "end": v(57.94, 5.95) * mm});
            skLineSegment(sketch, "E22.12.3.8", {"start": v(54.4, 9.49) * mm, "end": v(57.94, 5.95) * mm});
            skLineSegment(sketch, "E22.direction1", {"start": v(-57.11, 31) * mm, "end": v(-47.11, 31) * mm, "construction": true});
            skLineSegment(sketch, "E22.direction2", {"start": v(-57.11, 31) * mm, "end": v(-57.11, 21) * mm, "construction": true});
            skSolve(sketch);
        }
        {
            var Q0;
            Q0 = qSketchRegion(id + "F12", true);
            extrude(context, id + "F13", {"entities" : qUnion([Q0]), "operationType" : NewBodyOperationType.REMOVE, "endBound" : BoundingType.THROUGH_ALL, "oppositeDirection" : true, "depth" : 25 * mm, "offsetDistance" : 25 * mm, "hasSecondDirection" : true, "secondDirectionBound" : SecondDirectionBoundingType.THROUGH_ALL, "secondDirectionOppositeDirection" : false, "secondDirectionDepth" : 25 * mm});
        }
    });
